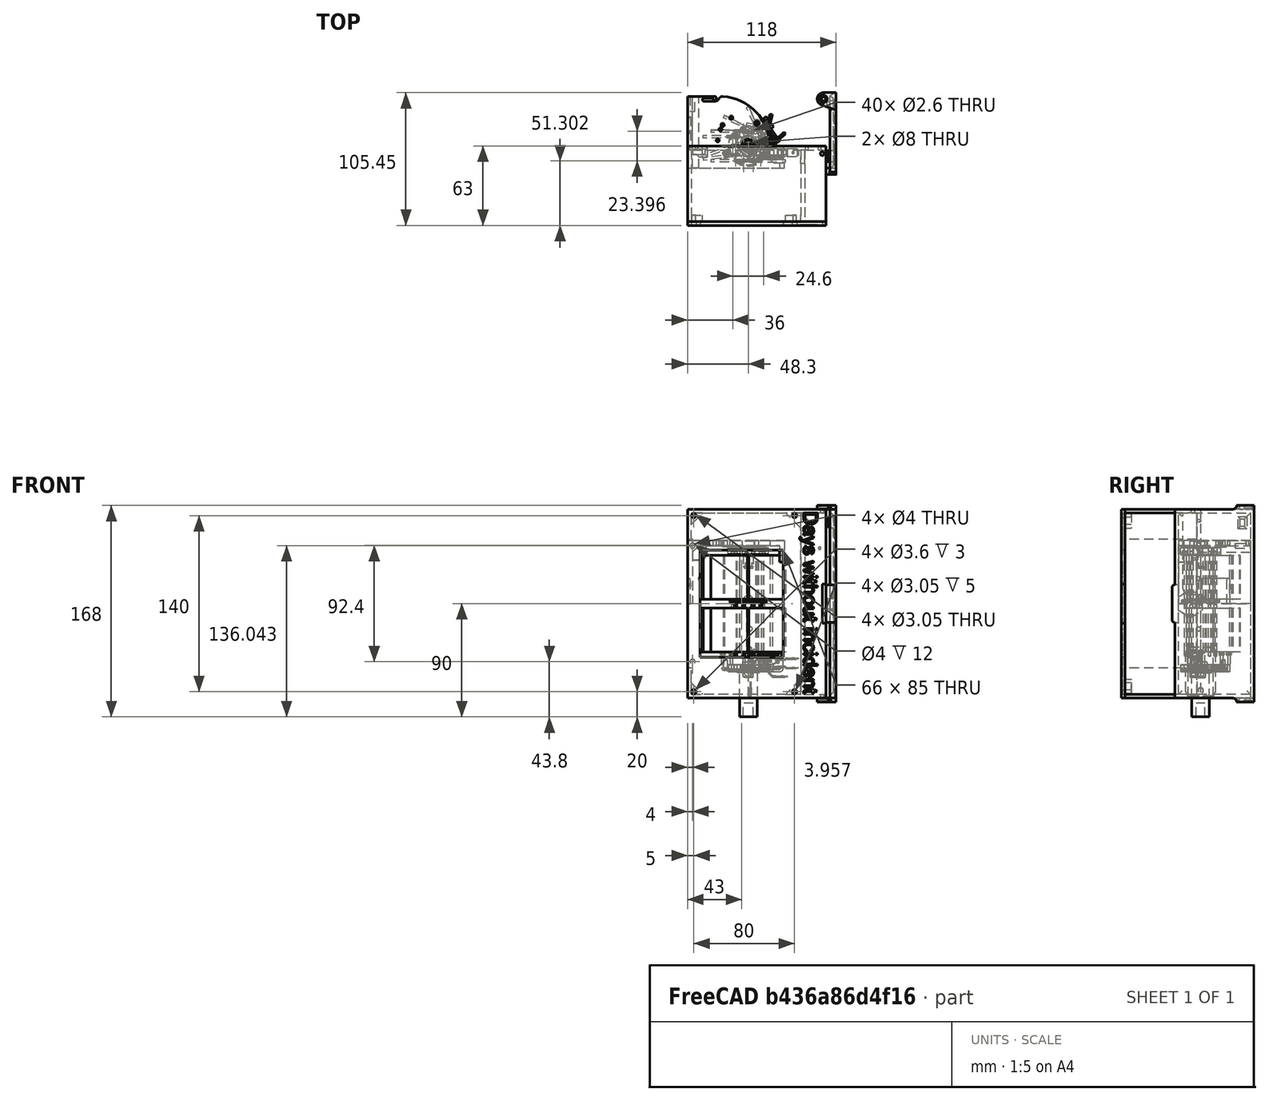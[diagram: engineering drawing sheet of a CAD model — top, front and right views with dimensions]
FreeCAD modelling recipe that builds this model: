
FCSTD DOCUMENT  (FreeCAD 1.0R39285 (Git))
Label: main
License: All rights reserved
LicenseURL: https://en.wikipedia.org/wiki/All_rights_reserved
objects: Sketcher::SketchObject×41, PartDesign::Pad×27, PartDesign::Body×22, Part::Feature×20, PartDesign::Chamfer×12, PartDesign::Pocket×12, App::Part×12, PartDesign::FeatureBase×11, Part::FeaturePython×8, PartDesign::Fillet×4, PartDesign::Revolution×3, PartDesign::Hole×3, PartDesign::PolarPattern×2, Mesh::Feature×1, PartDesign::Mirrored×1, Part::Part2DObjectPython×1, Part::Extrusion×1, PartDesign::LinearPattern×1
note: 347 computed .brp shape members not serialized (recipe doc carries the construction recipe); baked Part::Feature solids carry a one-line shape summary decoded from their .brp

FEATURE [Mesh::Feature] _8BYJ_48_stepper  label="28BYJ-48_stepper"
  Placement = pos=(-37.4756,7.81695,-15) rot=(0.862856,0.357407,0.357407;1.71777rad)
FEATURE [PartDesign::Body] Body  label="frame"
  AllowCompound = false
  Origin = -> Origin001
FEATURE [Sketcher::SketchObject] Sketch
  ArcFitTolerance = 1e-06
  AttachmentSupport = -> [XY_Plane001]
  FullyConstrained = true
  MakeInternals = false
  MapMode = 5
  sketch-geometry (33):
    g0: LineSegment StartX=0 StartY=0 StartZ=0 EndX=76.5 EndY=0 EndZ=0
    g1: LineSegment StartX=77 StartY=0.5 StartZ=0 EndX=77 EndY=3.5 EndZ=0
    g2: LineSegment [constr] StartX=25.5 StartY=57 StartZ=0 EndX=0 EndY=57 EndZ=0
    g3: LineSegment StartX=0 StartY=57 StartZ=0 EndX=0 EndY=0 EndZ=0
    g4: Circle CenterX=48.3 CenterY=17.5 CenterZ=0 NormalX=0 NormalY=0 NormalZ=1 AngleXU=0 Radius=4.8
    g5: Circle CenterX=30.2688 CenterY=10.7825 CenterZ=0 NormalX=0 NormalY=0 NormalZ=1 AngleXU=0 Radius=1.475
    g6: Circle CenterX=55.0175 CenterY=35.5312 CenterZ=0 NormalX=0 NormalY=0 NormalZ=1 AngleXU=0 Radius=1.475
    g7: LineSegment [constr] StartX=55.0175 StartY=35.5312 StartZ=0 EndX=30.2688 EndY=10.7825 EndZ=0
    g8: GeomPoint [constr] X=42.6431 Y=23.1569 Z=0
    g9: LineSegment [constr] StartX=42.6431 StartY=23.1569 StartZ=0 EndX=48.3 EndY=17.5 EndZ=0
    g10: LineSegment StartX=76.5 StartY=4 StartZ=0 EndX=70.5 EndY=4 EndZ=0
    g11: LineSegment StartX=65.5 StartY=9 StartZ=0 EndX=65.5 EndY=17 EndZ=0
    g12: ArcOfCircle CenterX=70.5 CenterY=9 CenterZ=0 NormalX=0 NormalY=0 NormalZ=1 AngleXU=0 Radius=5 StartAngle=3.14159 EndAngle=4.71239
    g13: GeomPoint [constr] X=65.5 Y=4 Z=0
    g14: ArcOfCircle CenterX=76.5 CenterY=0.5 CenterZ=0 NormalX=0 NormalY=0 NormalZ=1 AngleXU=0 Radius=0.5 StartAngle=4.71239 EndAngle=6.28319
    g15: GeomPoint [constr] X=77 Y=0 Z=0
    g16: ArcOfCircle CenterX=76.5 CenterY=3.5 CenterZ=0 NormalX=0 NormalY=0 NormalZ=1 AngleXU=0 Radius=0.5 StartAngle=0 EndAngle=1.5708
    g17: GeomPoint [constr] X=77 Y=4 Z=0
    g18: ArcOfCircle CenterX=25.5 CenterY=17 CenterZ=0 NormalX=0 NormalY=0 NormalZ=1 AngleXU=0 Radius=40 StartAngle=0 EndAngle=1.5708
    g19: GeomPoint [constr] X=65.5 Y=57 Z=0
    g20: Circle [constr] CenterX=55.0175 CenterY=35.5312 CenterZ=0 NormalX=0 NormalY=0 NormalZ=1 AngleXU=0 Radius=3.5
    g21: Circle [constr] CenterX=30.2688 CenterY=10.7825 CenterZ=0 NormalX=0 NormalY=0 NormalZ=1 AngleXU=0 Radius=3.5
    g22: Circle [constr] CenterX=42.6431 CenterY=23.1569 CenterZ=0 NormalX=0 NormalY=0 NormalZ=1 AngleXU=0 Radius=14
    g23: Circle CenterX=27.85 CenterY=34.05 CenterZ=0 NormalX=0 NormalY=0 NormalZ=1 AngleXU=0 Radius=1
    g24: Circle CenterX=34.7319 CenterY=39.85 CenterZ=0 NormalX=0 NormalY=0 NormalZ=1 AngleXU=0 Radius=1
    g25: Circle CenterX=24 CenterY=22 CenterZ=0 NormalX=0 NormalY=0 NormalZ=1 AngleXU=0 Radius=1
    g26: Circle CenterX=26.1879 CenterY=30.73 CenterZ=0 NormalX=0 NormalY=0 NormalZ=1 AngleXU=0 Radius=1
    g27: LineSegment StartX=20 StartY=55.5 StartZ=0 EndX=13 EndY=55.5 EndZ=0
    g28: ArcOfCircle CenterX=13 CenterY=54.3 CenterZ=0 NormalX=0 NormalY=0 NormalZ=1 AngleXU=0 Radius=1.2 StartAngle=1.5708 EndAngle=4.71239
    g29: LineSegment StartX=13 StartY=53.1 StartZ=0 EndX=21.6 EndY=53.1 EndZ=0
    g30: ArcOfCircle CenterX=21.6 CenterY=57 CenterZ=0 NormalX=0 NormalY=0 NormalZ=1 AngleXU=0 Radius=3.9 StartAngle=4.71239 EndAngle=6.28319
    g31: LineSegment StartX=21.5 StartY=57 StartZ=0 EndX=0 EndY=57 EndZ=0
    g32: ArcOfCircle CenterX=21.5 CenterY=55.5 CenterZ=0 NormalX=0 NormalY=0 NormalZ=1 AngleXU=0 Radius=1.5 StartAngle=3.14159 EndAngle=7.85399
  constraints (82):
    c: Coincident(g2,g3)
    c: Coincident(g3,g0)
    c: Horizontal(g0)
    c: Horizontal(g2)
    c: Vertical(g1)
    c: Vertical(g3)
    c: Distance(g15,g3) = 77
    c: Distance(g0,g2) = 57
    c: Coincident(g0,g-1)
    c: Diameter(g4) = 9.6
    c: Equal(g5,g6)
    c: Distance(g5,g6) = 35
    c: Coincident(g7,g6)
    c: Coincident(g7,g5)
    c: Symmetric(g7,g7,g8)
    c: Coincident(g9,g8)
    c: Coincident(g9,g4)
    c: Perpendicular(g7,g9)
    c: Distance(g9,g9) = 8
    c: Angle(g0,g7) = 0.785398
    c: Distance(g4,g3) = 48.3
    c: Distance(g4,g0) = 17.5
    c: Horizontal(g10)
    c: Vertical(g11)
    c: DistanceY(g15,g17) = 4
    c: DistanceX(g13,g17) = 11.5
    c: PointOnObject(g13,g10)
    c: PointOnObject(g13,g11)
    c: Tangent(g10,g12) = 1.5708
    c: Tangent(g11,g12) = 1.5708
    c: Radius(g12) = 5
    c: PointOnObject(g15,g0)
    c: PointOnObject(g15,g1)
    c: Tangent(g0,g14) = -1.5708
    c: Tangent(g1,g14) = -1.5708
    c: PointOnObject(g17,g1)
    c: PointOnObject(g17,g10)
    c: Tangent(g1,g16) = -1.5708
    c: Tangent(g10,g16) = -1.5708
    c: PointOnObject(g19,g2)
    c: PointOnObject(g19,g11)
    c: Tangent(g2,g18) = -1.5708
    c: Tangent(g11,g18) = -1.5708
    c: Coincident(g20,g6)
    c: Radius(g18) = 40
    c: Equal(g14,g16)
    c: Radius(g14) = 0.5
    c: Coincident(g21,g5)
    c: Diameter(g22) = 28
    c: Coincident(g22,g8)
    c: Diameter(g5) = 2.95
    c: Equal(g21,g20)
    c: Diameter(g21) = 7
    c: Diameter(g24) = 2
    c: Distance(g24,g23) = 9
    c: Distance(g23,g3) = 27.85
    c: Distance(g23,g0) = 34.05
    c: DistanceY(g23,g24) = 5.8
    c: Distance(g25,g26) = 9
    c: Equal(g24,g23)
    c: Equal(g23,g26)
    c: Equal(g26,g25)
    c: Distance(g25,g0) = 22
    c: Distance(g25,g3) = 24
    c: DistanceY(g25,g26) = 8.73
    c: PointOnObject(g31,g2)
    c: Horizontal(g27)
    c: Horizontal(g29)
    c: PointOnObject(g30,g2)
    c: Coincident(g30,g2)
    c: Tangent(g28,g27) = -1.5708
    c: Tangent(g29,g28) = -1.5708
    c: Tangent(g30,g29) = -1.5708
    c: Distance(g2,g27) = 1.5
    c: DistanceX(g27,g27) = 7
    c: Radius(g28) = 1.2
    c: DistanceX(g31,g2) = 4
    c: Coincident(g31,g2)
    c: Coincident(g32,g27)
    c: Coincident(g32,g31)
    c: Horizontal(g32,g27)
    c: Radius(g32) = 1.5
FEATURE [PartDesign::Pad] Pad  label="Face_Pad"
  Direction = (0,0,1)
  Length = 4
  Length2 = 10
  Profile = -> Sketch
  ReferenceAxis = -> Sketch [N_Axis]
  Refine = true
  Suppressed = false
  Type = 0
FEATURE [Sketcher::SketchObject] Sketch001
  ArcFitTolerance = 1e-06
  AttachmentSupport = -> [Pad]
  ExternalGeometry = -> [Pad]
  FullyConstrained = true
  MakeInternals = false
  MapMode = 5
  Placement = pos=(0,0,4) rot=(0,0,1;0rad)
  sketch-geometry (8):
    g0: LineSegment StartX=73 StartY=4 StartZ=0 EndX=73 EndY=0 EndZ=0
    g1: LineSegment StartX=73 StartY=0 StartZ=0 EndX=76.5 EndY=0 EndZ=0
    g2: LineSegment StartX=77 StartY=0.5 StartZ=0 EndX=77 EndY=3.5 EndZ=0
    g3: LineSegment StartX=76.5 StartY=4 StartZ=0 EndX=73 EndY=4 EndZ=0
    g4: ArcOfCircle CenterX=76.5 CenterY=3.5 CenterZ=0 NormalX=0 NormalY=0 NormalZ=1 AngleXU=0 Radius=0.5 StartAngle=2e-16 EndAngle=1.5708
    g5: GeomPoint [constr] X=77 Y=4 Z=0
    g6: ArcOfCircle CenterX=76.5 CenterY=0.5 CenterZ=0 NormalX=0 NormalY=0 NormalZ=1 AngleXU=0 Radius=0.5 StartAngle=4.71239 EndAngle=6.28319
    g7: GeomPoint [constr] X=77 Y=0 Z=0
  constraints (19):
    c: Coincident(g0,g1)
    c: Coincident(g3,g0)
    c: Vertical(g0)
    c: Vertical(g2)
    c: Horizontal(g1)
    c: Horizontal(g3)
    c: PointOnObject(g7,g-1)
    c: PointOnObject(g-4,g2)
    c: DistanceX(g3,g5) = 4
    c: PointOnObject(g5,g2)
    c: PointOnObject(g5,g3)
    c: Tangent(g2,g4) = -1.5708
    c: Tangent(g3,g4) = -1.5708
    c: PointOnObject(g7,g1)
    c: PointOnObject(g7,g2)
    c: Tangent(g1,g6) = -1.5708
    c: Tangent(g2,g6) = -1.5708
    c: Equal(g4,g6)
    c: Coincident(g3,g-3)
FEATURE [PartDesign::Pad] Pad001  label="TopStopper_Pad"
  Direction = (0,0,1)
  Length = 13
  Length2 = 10
  Profile = -> Sketch001
  ReferenceAxis = -> Sketch001 [N_Axis]
  Refine = true
  Suppressed = false
  Type = 0
FEATURE [Sketcher::SketchObject] Sketch002
  ArcFitTolerance = 1e-06
  AttachmentSupport = -> [Pad]
  FullyConstrained = true
  MakeInternals = false
  MapMode = 5
  Placement = pos=(0,0,4) rot=(0,0,1;0rad)
  sketch-geometry (4):
    g0: LineSegment StartX=0 StartY=11 StartZ=0 EndX=14 EndY=11 EndZ=0
    g1: LineSegment StartX=14 StartY=11 StartZ=0 EndX=14 EndY=15 EndZ=0
    g2: LineSegment StartX=14 StartY=15 StartZ=0 EndX=0 EndY=15 EndZ=0
    g3: LineSegment StartX=0 StartY=15 StartZ=0 EndX=0 EndY=11 EndZ=0
  constraints (12):
    c: Coincident(g0,g1)
    c: Coincident(g1,g2)
    c: Coincident(g2,g3)
    c: Coincident(g3,g0)
    c: Horizontal(g0)
    c: Horizontal(g2)
    c: Vertical(g1)
    c: Vertical(g3)
    c: Distance(g1,g3) = 14
    c: Distance(g0,g2) = 4
    c: PointOnObject(g0,g-2)
    c: Distance(g-1,g0) = 11
FEATURE [PartDesign::Pad] Pad002  label="BottomStopper_Pad"
  Direction = (0,0,1)
  Length = 11.5
  Length2 = 10
  Profile = -> Sketch002
  ReferenceAxis = -> Sketch002 [N_Axis]
  Refine = true
  Suppressed = false
  Type = 0
FEATURE [PartDesign::Chamfer] Chamfer  label="BottomStopper_Chamfer"
  Angle = 45
  Base = -> Pad002 [Edge3,Edge6,Edge9,Edge7]
  ChamferType = 0
  FlipDirection = false
  Refine = true
  Size = 2
  Size2 = 1
  SupportTransform = false
  Suppressed = false
  UseAllEdges = false
FEATURE [Sketcher::SketchObject] Sketch003
  ArcFitTolerance = 1e-06
  AttachmentSupport = -> [Chamfer]
  ExternalGeometry = -> [Chamfer]
  FullyConstrained = true
  MakeInternals = false
  MapMode = 5
  Placement = pos=(0,0,4) rot=(0,0,1;0rad)
  sketch-geometry (4):
    g0: LineSegment StartX=0 StartY=0 StartZ=0 EndX=4 EndY=0 EndZ=0
    g1: LineSegment StartX=4 StartY=0 StartZ=0 EndX=4 EndY=57 EndZ=0
    g2: LineSegment StartX=4 StartY=57 StartZ=0 EndX=0 EndY=57 EndZ=0
    g3: LineSegment StartX=0 StartY=57 StartZ=0 EndX=0 EndY=0 EndZ=0
  constraints (11):
    c: Coincident(g0,g1)
    c: Coincident(g1,g2)
    c: Coincident(g2,g3)
    c: Coincident(g3,g0)
    c: Horizontal(g0)
    c: Horizontal(g2)
    c: Vertical(g1)
    c: Vertical(g3)
    c: Coincident(g0,g-1)
    c: PointOnObject(g1,g-3)
    c: DistanceX(g2,g2) = 4
FEATURE [PartDesign::Pad] Pad003  label="Bottom_Pad"
  Direction = (0,0,1)
  Length = 46
  Length2 = 10
  Profile = -> Sketch003
  ReferenceAxis = -> Sketch003 [N_Axis]
  Refine = true
  Suppressed = false
  Type = 0
FEATURE [PartDesign::Chamfer] Chamfer001  label="Bottom_Chamfer"
  Angle = 45
  Base = -> Pad003 [Edge4,Edge17]
  ChamferType = 0
  FlipDirection = false
  Refine = true
  Size = 5
  Size2 = 1
  SupportTransform = false
  Suppressed = false
  UseAllEdges = false
FEATURE [Sketcher::SketchObject] Sketch004
  ArcFitTolerance = 1e-06
  AttachmentSupport = -> [XY_Plane003]
  FullyConstrained = true
  MakeInternals = false
  MapMode = 5
  sketch-geometry (6):
    g0: LineSegment StartX=0 StartY=0 StartZ=0 EndX=12 EndY=0 EndZ=0
    g1: LineSegment StartX=12 StartY=0 StartZ=0 EndX=12 EndY=10 EndZ=0
    g2: LineSegment StartX=12 StartY=10 StartZ=0 EndX=0 EndY=10 EndZ=0
    g3: LineSegment StartX=0 StartY=10 StartZ=0 EndX=0 EndY=0 EndZ=0
    g4: Circle CenterX=2.05 CenterY=2.17159 CenterZ=0 NormalX=0 NormalY=0 NormalZ=1 AngleXU=0 Radius=1.05
    g5: Circle CenterX=8.95 CenterY=7.95 CenterZ=0 NormalX=0 NormalY=0 NormalZ=1 AngleXU=0 Radius=1.05
  constraints (17):
    c: Coincident(g0,g1)
    c: Coincident(g1,g2)
    c: Coincident(g2,g3)
    c: Coincident(g3,g0)
    c: Horizontal(g0)
    c: Horizontal(g2)
    c: Vertical(g1)
    c: Vertical(g3)
    c: Distance(g1,g3) = 12
    c: Distance(g0,g2) = 10
    c: Coincident(g0,g-1)
    c: Equal(g5,g4)
    c: Diameter(g4) = 2.1
    c: Distance(g4,g5) = 9
    c: Distance(g5,g1) = 2
    c: Distance(g5,g2) = 1
    c: Distance(g4,g3) = 1
FEATURE [PartDesign::Pad] Pad004  label="Body_Pad"
  Direction = (0,0,1)
  Length = 5.4
  Length2 = 10
  Profile = -> Sketch004
  ReferenceAxis = -> Sketch004 [N_Axis]
  Refine = true
  Suppressed = false
  Type = 0
FEATURE [Sketcher::SketchObject] Sketch005
  ArcFitTolerance = 1e-06
  AttachmentSupport = -> [XY_Plane003]
  ExternalGeometry = -> [Pad004]
  FullyConstrained = true
  MakeInternals = false
  MapMode = 5
  sketch-geometry (6):
    g0: LineSegment StartX=-4.24264 StartY=12.8284 StartZ=0 EndX=0.353553 EndY=8.23223 EndZ=0
    g1: LineSegment StartX=0.353553 StartY=8.23223 StartZ=0 EndX=1.76777 EndY=9.64645 EndZ=0
    g2: LineSegment StartX=1.76777 StartY=9.64645 StartZ=0 EndX=-2.82843 EndY=14.2426 EndZ=0
    g3: ArcOfCircle CenterX=-3.53553 CenterY=13.5355 CenterZ=0 NormalX=0 NormalY=0 NormalZ=1 AngleXU=0 Radius=1 StartAngle=0.785398 EndAngle=3.92699
    g4: GeomPoint X=1.06066 Y=8.93934 Z=0
    g5: LineSegment [constr] StartX=0 StartY=10 StartZ=0 EndX=1.06066 EndY=8.93934 EndZ=0
  constraints (14):
    c: Coincident(g0,g1)
    c: Coincident(g1,g2)
    c: Tangent(g3,g0) = -1.5708
    c: Tangent(g3,g2) = -1.5708
    c: Equal(g0,g2)
    c: Radius(g3) = 1
    c: Parallel(g0,g2)
    c: Angle(g-2,g2) = 0.785398
    c: Distance(g2,g2) = 6.5
    c: Symmetric(g1,g1,g4)
    c: Coincident(g5,g-3)
    c: Coincident(g5,g4)
    c: Distance(g5,g5) = 1.5
    c: Angle(g-2,g5) = 0.785398
FEATURE [PartDesign::Pad] Pad005  label="LeverOFF_Pad"
  BaseFeature = -> Pad004
  Direction = (0,0,1)
  Length = 4.4
  Length2 = -1
  Profile = -> Sketch005
  ReferenceAxis = -> Sketch005 [N_Axis]
  Refine = true
  Suppressed = false
  Type = 4
FEATURE [Sketcher::SketchObject] Sketch006
  ArcFitTolerance = 1e-06
  AttachmentSupport = -> [Pad005]
  ExternalGeometry = -> [Pad005]
  FullyConstrained = true
  MakeInternals = false
  MapMode = 5
  Placement = pos=(0,0,0) rot=(1,0,0;1.5708rad)
  sketch-geometry (6):
    g0: GeomPoint X=12 Y=2.7 Z=0
    g1: LineSegment [constr] StartX=12 StartY=2.7 StartZ=0 EndX=0 EndY=2.7 EndZ=0
    g2: Circle CenterX=3.5 CenterY=2.7 CenterZ=0 NormalX=0 NormalY=0 NormalZ=1 AngleXU=0 Radius=1
    g3: Circle CenterX=6 CenterY=2.7 CenterZ=0 NormalX=0 NormalY=0 NormalZ=1 AngleXU=0 Radius=1
    g4: Circle CenterX=8.5 CenterY=2.7 CenterZ=0 NormalX=0 NormalY=0 NormalZ=1 AngleXU=0 Radius=1
    g5: GeomPoint X=6 Y=2.7 Z=0
  constraints (13):
    c: Symmetric(g-3,g-3,g0)
    c: Coincident(g1,g0)
    c: Horizontal(g1)
    c: Diameter(g2) = 2
    c: PointOnObject(g2,g1)
    c: PointOnObject(g4,g1)
    c: Equal(g4,g3)
    c: Equal(g3,g2)
    c: DistanceX(g2,g3) = 2.5
    c: DistanceX(g3,g4) = 2.5
    c: Symmetric(g1,g1,g5)
    c: Coincident(g5,g3)
    c: PointOnObject(g1,g-2)
FEATURE [PartDesign::Pad] Pad006  label="Wires_Pad"
  BaseFeature = -> Pad005
  Direction = (0,-1,2e-16)
  Length = 12
  Length2 = 10
  Profile = -> Sketch006
  ReferenceAxis = -> Sketch006 [N_Axis]
  Refine = true
  Suppressed = false
  Type = 0
FEATURE [Sketcher::SketchObject] Sketch007
  ArcFitTolerance = 1e-06
  AttachmentSupport = -> [XY_Plane003]
  ExternalGeometry = -> [Pad004]
  FullyConstrained = true
  MakeInternals = false
  MapMode = 5
  sketch-geometry (6):
    g0: LineSegment StartX=1.06066 StartY=7.93934 StartZ=0 EndX=-5.43934 EndY=7.93934 EndZ=0
    g1: LineSegment StartX=-5.43934 StartY=9.93934 StartZ=0 EndX=1.06066 EndY=9.93934 EndZ=0
    g2: LineSegment StartX=1.06066 StartY=7.93934 StartZ=0 EndX=1.06066 EndY=9.93934 EndZ=0
    g3: ArcOfCircle CenterX=-5.43934 CenterY=8.93934 CenterZ=0 NormalX=0 NormalY=0 NormalZ=1 AngleXU=0 Radius=1 StartAngle=1.5708 EndAngle=4.71239
    g4: LineSegment [constr] StartX=0 StartY=10 StartZ=0 EndX=1.06066 EndY=8.93934 EndZ=0
    g5: GeomPoint [constr] X=1.06066 Y=8.93934 Z=0
  constraints (14):
    c: Horizontal(g0)
    c: Horizontal(g1)
    c: Coincident(g2,g0)
    c: Coincident(g2,g1)
    c: Vertical(g2)
    c: Tangent(g3,g1) = 1.5708
    c: Tangent(g3,g0) = 1.5708
    c: Radius(g3) = 1
    c: DistanceX(g1,g1) = 6.5
    c: Distance(g4) = 1.5
    c: Angle(g-1,g4) = -0.785398
    c: Coincident(g4,g-3)
    c: Symmetric(g2,g2,g5)
    c: Coincident(g5,g4)
FEATURE [PartDesign::Pad] Pad007  label="LeverON_Pad"
  BaseFeature = -> Pad006
  Direction = (0,0,1)
  Length = 4.4
  Length2 = -1
  Profile = -> Sketch007
  ReferenceAxis = -> Sketch007 [N_Axis]
  Refine = true
  Suppressed = false
  Type = 4
FEATURE [PartDesign::Body] Body001  label="Body"
  AllowCompound = false
  Group = -> [Sketch004,Pad004,Sketch005,Pad005,Sketch006,Pad006,Sketch007,Pad007]
  Origin = -> Origin003
  Tip = -> Pad007
FEATURE [Sketcher::SketchObject] Sketch008
  ArcFitTolerance = 1e-06
  AttachmentSupport = -> [XY_Plane005]
  FullyConstrained = true
  MakeInternals = false
  MapMode = 5
  sketch-geometry (6):
    g0: Circle CenterX=0 CenterY=0 CenterZ=0 NormalX=0 NormalY=0 NormalZ=1 AngleXU=0 Radius=16
    g1: LineSegment StartX=-2.55 StartY=-1.55 StartZ=0 EndX=2.55 EndY=-1.55 EndZ=0
    g2: LineSegment StartX=2.55 StartY=-1.55 StartZ=0 EndX=2.55 EndY=1.55 EndZ=0
    g3: LineSegment StartX=2.55 StartY=1.55 StartZ=0 EndX=-2.55 EndY=1.55 EndZ=0
    g4: LineSegment StartX=-2.55 StartY=1.55 StartZ=0 EndX=-2.55 EndY=-1.55 EndZ=0
    g5: GeomPoint [constr] X=0 Y=0 Z=0
  constraints (14):
    c: Coincident(g0,g-1)
    c: Coincident(g1,g2)
    c: Coincident(g2,g3)
    c: Coincident(g3,g4)
    c: Coincident(g4,g1)
    c: Horizontal(g1)
    c: Horizontal(g3)
    c: Vertical(g2)
    c: Vertical(g4)
    c: Symmetric(g3,g1,g5)
    c: Distance(g2,g4) = 5.1
    c: Distance(g1,g3) = 3.1
    c: Coincident(g5,g0)
    c: Diameter(g0) = 32
FEATURE [PartDesign::Pad] Pad008  label="Flange_Pad001"
  Direction = (0,0,1)
  Length = 5.5
  Length2 = 10
  Profile = -> Sketch008
  ReferenceAxis = -> Sketch008 [N_Axis]
  Refine = true
  Suppressed = false
  Type = 0
FEATURE [Sketcher::SketchObject] Sketch009
  ArcFitTolerance = 1e-06
  AttachmentSupport = -> [Chamfer001]
  ExternalGeometry = -> [Chamfer001]
  FullyConstrained = true
  MakeInternals = false
  MapMode = 5
  Placement = pos=(0,0,4) rot=(0,0,1;0rad)
  sketch-geometry (2):
    g0: Circle CenterX=48.3 CenterY=17.5 CenterZ=0 NormalX=0 NormalY=0 NormalZ=1 AngleXU=0 Radius=4.8
    g1: Circle CenterX=48.3 CenterY=17.5 CenterZ=0 NormalX=0 NormalY=0 NormalZ=1 AngleXU=0 Radius=7.3
  constraints (4):
    c: Coincident(g0,g-3)
    c: Equal(g0,g-3)
    c: Coincident(g1,g0)
    c: Distance(g0,g1) = 2.5
FEATURE [PartDesign::Pad] Pad009  label="Flange_Pad"
  Direction = (0,0,1)
  Length = 1.75
  Length2 = 10
  Profile = -> Sketch009
  ReferenceAxis = -> Sketch009 [N_Axis]
  Refine = true
  Suppressed = false
  Type = 0
FEATURE [PartDesign::Chamfer] Chamfer002  label="Flange_Chamfer"
  Angle = 45
  Base = -> Pad009 [Edge76,Edge107,Edge20,Edge103]
  ChamferType = 0
  FlipDirection = false
  Refine = true
  Size = 0.5
  Size2 = 1
  SupportTransform = false
  Suppressed = false
  UseAllEdges = false
FEATURE [Sketcher::SketchObject] Sketch010
  ArcFitTolerance = 1e-06
  AttachmentSupport = -> [Pad008]
  FullyConstrained = true
  MakeInternals = false
  MapMode = 5
  Placement = pos=(0,0,5.5) rot=(0,0,1;0rad)
  sketch-geometry (1):
    g0: Circle CenterX=12.3 CenterY=0 CenterZ=0 NormalX=0 NormalY=0 NormalZ=1 AngleXU=0 Radius=1.3
  constraints (3):
    c: Diameter(g0) = 2.6
    c: PointOnObject(g0,g-1)
    c: Distance(g-1,g0) = 11
FEATURE [PartDesign::Pocket] Pocket  label="Flap_Pocket"
  BaseFeature = -> Pad008
  Direction = (0,0,-1)
  Length = 5
  Length2 = 5
  Profile = -> Sketch010
  ReferenceAxis = -> Sketch010 [N_Axis]
  Refine = true
  Suppressed = false
  Type = 2
FEATURE [PartDesign::Chamfer] Chamfer003  label="FlapHole_Chamfer"
  Angle = 45
  Base = -> Pocket [Edge13,Edge8]
  BaseFeature = -> Pocket
  ChamferType = 0
  FlipDirection = false
  Refine = true
  Size = 0.2
  Size2 = 1
  SupportTransform = false
  Suppressed = false
  UseAllEdges = false
FEATURE [PartDesign::PolarPattern] PolarPattern  label="Flap_PolarPattern"
  Angle = 360
  Axis = -> Z_Axis005
  BaseFeature = -> Chamfer003
  Mode = 0
  Occurrences = 10
  Offset = 120
  Originals = -> [Pocket,Chamfer003]
  Refine = true
  Suppressed = false
  TransformMode = 0
FEATURE [PartDesign::FeatureBase] Clone
  BaseFeature = -> Body001
  Suppressed = false
FEATURE [PartDesign::Body] Body003  label="Copy"
  AllowCompound = false
  Group = -> [Clone]
  Origin = -> Origin006
  Placement = pos=(10.2368,8.31942,0) rot=(0,0,-1;5.65487rad)
  Tip = -> Clone
FEATURE [App::Part] Part001  label="MicroSW"
  Group = -> [Body001,Body003]
  Origin = -> Origin002
  Placement = pos=(-11.5,24.5,8) rot=(0,0,-1;3.14159rad)
FEATURE [Sketcher::SketchObject] Sketch012
  ArcFitTolerance = 1e-06
  AttachmentSupport = -> [Chamfer002]
  ExternalGeometry = -> [Chamfer002]
  FullyConstrained = true
  MakeInternals = false
  MapMode = 5
  Placement = pos=(0,0,4) rot=(0,0,1;0rad)
  sketch-geometry (4):
    g0: Circle CenterX=55.0175 CenterY=35.5312 CenterZ=0 NormalX=0 NormalY=0 NormalZ=1 AngleXU=0 Radius=1.525
    g1: Circle CenterX=55.0175 CenterY=35.5312 CenterZ=0 NormalX=0 NormalY=0 NormalZ=1 AngleXU=0 Radius=2.525
    g2: Circle CenterX=30.2688 CenterY=10.7825 CenterZ=0 NormalX=0 NormalY=0 NormalZ=1 AngleXU=0 Radius=1.525
    g3: Circle CenterX=30.2688 CenterY=10.7825 CenterZ=0 NormalX=0 NormalY=0 NormalZ=1 AngleXU=0 Radius=2.525
  constraints (8):
    c: Coincident(g0,g-4)
    c: Equal(g0,g-4)
    c: Coincident(g1,g0)
    c: Coincident(g2,g-3)
    c: Equal(g2,g-3)
    c: Coincident(g3,g2)
    c: Equal(g3,g1)
    c: Distance(g0,g1) = 1
FEATURE [PartDesign::Pad] Pad010  label="MotorHole_Pad"
  Direction = (0,0,1)
  Length = 1
  Length2 = 10
  Profile = -> Sketch012
  ReferenceAxis = -> Sketch012 [N_Axis]
  Refine = true
  Suppressed = false
  Type = 0
FEATURE [PartDesign::Chamfer] Chamfer005  label="TinyHoles_Chamfer"
  Angle = 45
  Base = -> Pad010 [Edge19,Edge21,Edge22,Edge23,Edge24,Edge18,Edge72,Edge84,Edge74,Edge104,Edge105,Edge82,Edge80,Edge78]
  ChamferType = 0
  FlipDirection = false
  Refine = true
  Size = 0.2
  Size2 = 1
  SupportTransform = false
  Suppressed = false
  UseAllEdges = false
FEATURE [Sketcher::SketchObject] Sketch013
  ArcFitTolerance = 1e-06
  AttachmentSupport = -> [Chamfer005]
  ExternalGeometry = -> [Chamfer005]
  FullyConstrained = true
  MakeInternals = false
  MapMode = 5
  Placement = pos=(0,0,50) rot=(0,0,1;0rad)
  sketch-geometry (6):
    g0: GeomPoint X=0 Y=28.5 Z=0
    g1: LineSegment StartX=0 StartY=38.5 StartZ=0 EndX=0 EndY=18.5 EndZ=0
    g2: GeomPoint X=0 Y=28.5 Z=0
    g3: LineSegment StartX=0 StartY=38.5 StartZ=0 EndX=2.5 EndY=41 EndZ=0
    g4: LineSegment StartX=2.5 StartY=41 StartZ=0 EndX=2.5 EndY=16 EndZ=0
    g5: LineSegment StartX=2.5 StartY=16 StartZ=0 EndX=0 EndY=18.5 EndZ=0
  constraints (13):
    c: Symmetric(g-3,g-3,g0)
    c: PointOnObject(g1,g-3)
    c: Symmetric(g1,g1,g2)
    c: Coincident(g2,g0)
    c: Coincident(g3,g1)
    c: Coincident(g4,g3)
    c: Vertical(g4)
    c: Coincident(g5,g4)
    c: Coincident(g5,g1)
    c: Equal(g5,g3)
    c: Distance(g4,g1) = 2.5
    c: Angle(g4,g5) = 0.785398
    c: DistanceY(g4,g4) = 25
FEATURE [PartDesign::Pocket] Pocket002  label="LeftRightJoint_Pocket"
  Direction = (0,0,-1)
  Length = 20
  Length2 = 5
  Profile = -> Sketch013
  ReferenceAxis = -> Sketch013 [N_Axis]
  Refine = true
  Suppressed = false
  Type = 0
FEATURE [Sketcher::SketchObject] Sketch014
  ArcFitTolerance = 1e-06
  AttachmentOffset = pos=(0,0,-1) rot=(0,0,1;0rad)
  AttachmentSupport = -> [Pocket002]
  ExternalGeometry = -> [Pocket002]
  FullyConstrained = true
  MakeInternals = false
  MapMode = 5
  Placement = pos=(3.5,0,0) rot=(0.57735,-0.57735,-0.57735;2.0944rad)
  sketch-geometry (5):
    g0: GeomPoint X=-28.5 Y=50 Z=0
    g1: LineSegment [constr] StartX=-28.5 StartY=50 StartZ=0 EndX=-28.5 EndY=35 EndZ=0
    g2: LineSegment StartX=-28.5 StartY=37 StartZ=0 EndX=-28.5 EndY=33 EndZ=0
    g3: GeomPoint X=-28.5 Y=35 Z=0
    g4: ArcOfCircle CenterX=-28.5 CenterY=35 CenterZ=0 NormalX=0 NormalY=0 NormalZ=1 AngleXU=0 Radius=2 StartAngle=1.5708 EndAngle=4.71239
  constraints (11):
    c: Symmetric(g-3,g-3,g0)
    c: Distance(g1) = 15
    c: Coincident(g1,g0)
    c: Vertical(g1)
    c: PointOnObject(g2,g1)
    c: Symmetric(g2,g2,g3)
    c: Coincident(g3,g1)
    c: DistanceY(g2,g2) = 4
    c: Coincident(g4,g2)
    c: Coincident(g4,g1)
    c: PointOnObject(g4,g1)
FEATURE [PartDesign::Revolution] Revolution  label="JointIndent_Revolution"
  Angle = 180
  Angle2 = 60
  Axis = (0,0,-15)
  Base = (3.5,28.5,50)
  Profile = -> Sketch014
  ReferenceAxis = -> Sketch014 [Axis]
  Refine = true
  Reversed = true
  Suppressed = false
  Type = 0
FEATURE [Sketcher::SketchObject] Sketch015
  ArcFitTolerance = 1e-06
  AttachmentSupport = -> [XY_Plane008]
  FullyConstrained = true
  MakeInternals = false
  MapMode = 5
  expr: Constraints[21] = 25 / 2 - 0.1
  sketch-geometry (9):
    g0: LineSegment StartX=4.47e-14 StartY=-10.1 StartZ=0 EndX=-4.52e-14 EndY=10.1 EndZ=0
    g1: LineSegment StartX=-4.52e-14 StartY=10.1 StartZ=0 EndX=1.8 EndY=11.9 EndZ=0
    g2: LineSegment StartX=1.8 StartY=11.9 StartZ=0 EndX=2.3 EndY=11.9 EndZ=0
    g3: LineSegment StartX=2.3 StartY=11.9 StartZ=0 EndX=2.3 EndY=-11.9 EndZ=0
    g4: LineSegment StartX=2.3 StartY=-11.9 StartZ=0 EndX=1.8 EndY=-11.9 EndZ=0
    g5: LineSegment StartX=1.8 StartY=-11.9 StartZ=0 EndX=4.46e-14 EndY=-10.1 EndZ=0
    g6: GeomPoint X=-3e-16 Y=-2.8e-15 Z=0
    g7: LineSegment [constr] StartX=1.8 StartY=-11.9 StartZ=0 EndX=2.3 EndY=-12.4 EndZ=0
    g8: LineSegment [constr] StartX=2.3 StartY=-11.9 StartZ=0 EndX=2.3 EndY=-12.4 EndZ=0
  constraints (24):
    c: PointOnObject(g0,g-2)
    c: PointOnObject(g0,g-2)
    c: Coincident(g0,g1)
    c: Coincident(g1,g2)
    c: Horizontal(g2)
    c: Coincident(g2,g3)
    c: Vertical(g3)
    c: Coincident(g3,g4)
    c: Coincident(g4,g5)
    c: Coincident(g5,g0)
    c: Horizontal(g4)
    c: Equal(g2,g4)
    c: Equal(g5,g1)
    c: Angle(g1,g3) = 0.785398
    c: Symmetric(g0,g0,g6)
    c: Distance(g4,g4) = 0.5
    c: Coincident(g7,g4)
    c: Coincident(g8,g7)
    c: Vertical(g8)
    c: Parallel(g7,g5)
    c: Coincident(g8,g3)
    c: DistanceY(g7,g6) = 12.4
    c: Distance(g3,g0) = 2.3
    c: PointOnObject(g6,g-1)
FEATURE [PartDesign::Pad] Pad011
  Direction = (0,0,1)
  Length = 39
  Length2 = 10
  Midplane = true
  Profile = -> Sketch015
  ReferenceAxis = -> Sketch015 [N_Axis]
  Refine = true
  Suppressed = false
  Type = 0
FEATURE [Sketcher::SketchObject] Sketch016
  ArcFitTolerance = 1e-06
  AttachmentSupport = -> [Pad011]
  FullyConstrained = true
  MakeInternals = false
  MapMode = 5
  Placement = pos=(2.3,0,0) rot=(0.57735,0.57735,0.57735;2.0944rad)
  sketch-geometry (2):
    g0: Circle CenterX=0 CenterY=15 CenterZ=0 NormalX=0 NormalY=0 NormalZ=1 AngleXU=0 Radius=2
    g1: Circle CenterX=0 CenterY=-15 CenterZ=0 NormalX=0 NormalY=0 NormalZ=1 AngleXU=0 Radius=2
  constraints (5):
    c: Diameter(g0) = 4
    c: PointOnObject(g0,g-2)
    c: Diameter(g1) = 4
    c: Symmetric(g0,g1,g-1)
    c: Distance(g1,g-1) = 15
FEATURE [PartDesign::Pocket] Pocket003
  BaseFeature = -> Pad011
  Direction = (-1,0,0)
  Length = 5
  Length2 = 5
  Profile = -> Sketch016
  ReferenceAxis = -> Sketch016 [N_Axis]
  Refine = true
  Suppressed = false
  Type = 2
FEATURE [PartDesign::Chamfer] Chamfer006
  Angle = 45
  Base = -> Pocket003 [Edge13,Edge11,Edge17,Edge15]
  BaseFeature = -> Pocket003
  ChamferType = 1
  FlipDirection = false
  Refine = true
  Size = 1.5
  Size2 = 4
  SupportTransform = false
  Suppressed = false
  UseAllEdges = false
FEATURE [PartDesign::Chamfer] Chamfer007
  Angle = 45
  Base = -> Chamfer006 [Edge29,Edge24,Edge28,Edge23]
  BaseFeature = -> Chamfer006
  ChamferType = 0
  FlipDirection = false
  Refine = true
  Size = 0.2
  Size2 = 1
  SupportTransform = false
  Suppressed = false
  UseAllEdges = false
FEATURE [PartDesign::Body] Body004
  AllowCompound = false
  Group = -> [Sketch015,Pad011,Sketch016,Pocket003,Chamfer006,Chamfer007]
  Origin = -> Origin008
  Tip = -> Chamfer007
FEATURE [App::Part] Part003  label="JointKey"
  Group = -> [Body004]
  Origin = -> Origin007
  Placement = pos=(-48.1,11,54) rot=(0,0,1;0rad)
FEATURE [Sketcher::SketchObject] Sketch017
  ArcFitTolerance = 1e-06
  AttachmentSupport = -> [XY_Plane010]
  FullyConstrained = true
  MakeInternals = false
  MapMode = 5
  sketch-geometry (1):
    g0: Circle CenterX=0 CenterY=0 CenterZ=0 NormalX=0 NormalY=0 NormalZ=1 AngleXU=0 Radius=15
  constraints (2):
    c: Diameter(g0) = 30
    c: Coincident(g0,g-1)
FEATURE [PartDesign::Pad] Pad012  label="Base_Pad"
  Direction = (0,0,1)
  Length = 2
  Length2 = 10
  Profile = -> Sketch017
  ReferenceAxis = -> Sketch017 [N_Axis]
  Refine = true
  Suppressed = false
  Type = 0
FEATURE [Sketcher::SketchObject] Sketch018
  ArcFitTolerance = 1e-06
  AttachmentSupport = -> [Pad012]
  FullyConstrained = true
  MakeInternals = false
  MapMode = 5
  Placement = pos=(0,0,0) rot=(1,0,0;3.14159rad)
  sketch-geometry (1):
    g0: Circle CenterX=12.3 CenterY=0 CenterZ=0 NormalX=0 NormalY=0 NormalZ=1 AngleXU=0 Radius=1.3
  constraints (3):
    c: Diameter(g0) = 2.6
    c: PointOnObject(g0,g-1)
    c: Distance(g-1,g0) = 11
FEATURE [PartDesign::Pocket] Pocket004  label="Flap_Pocket001"
  BaseFeature = -> Pad012
  Direction = (0,0,1)
  Length = 5
  Length2 = 5
  Profile = -> Sketch018
  ReferenceAxis = -> Sketch018 [N_Axis]
  Refine = true
  Suppressed = false
  Type = 2
FEATURE [PartDesign::Chamfer] Chamfer008  label="FlapPocket_Chamfer"
  Angle = 45
  Base = -> Pocket004 [Edge4,Edge5]
  BaseFeature = -> Pocket004
  ChamferType = 0
  FlipDirection = false
  Refine = true
  Size = 0.2
  Size2 = 1
  SupportTransform = false
  Suppressed = false
  UseAllEdges = false
FEATURE [PartDesign::PolarPattern] PolarPattern001  label="Flap_PolarPattern001"
  Angle = 360
  Axis = -> Z_Axis010
  BaseFeature = -> Chamfer008
  Mode = 0
  Occurrences = 10
  Offset = 120
  Originals = -> [Pocket004,Chamfer008]
  Refine = true
  Suppressed = false
  TransformMode = 0
FEATURE [Sketcher::SketchObject] Sketch019
  ArcFitTolerance = 1e-06
  AttachmentSupport = -> [PolarPattern001]
  FullyConstrained = true
  MakeInternals = false
  MapMode = 5
  Placement = pos=(0,0,0) rot=(1,0,0;3.14159rad)
  sketch-geometry (1):
    g0: Circle CenterX=0 CenterY=0 CenterZ=0 NormalX=0 NormalY=0 NormalZ=1 AngleXU=0 Radius=7
  constraints (2):
    c: Diameter(g0) = 14
    c: Coincident(g0,g-1)
FEATURE [PartDesign::Pad] Pad013  label="Shaft_Pad"
  BaseFeature = -> PolarPattern001
  Direction = (0,0,-1)
  Length = 36
  Length2 = 10
  Profile = -> Sketch019
  ReferenceAxis = -> Sketch019 [N_Axis]
  Refine = true
  Suppressed = false
  Type = 0
FEATURE [Sketcher::SketchObject] Sketch021
  ArcFitTolerance = 1e-06
  AttachmentSupport = -> [Pad013]
  FullyConstrained = true
  MakeInternals = false
  MapMode = 5
  Placement = pos=(0,0,-36) rot=(1,0,0;3.14159rad)
  sketch-geometry (5):
    g0: LineSegment StartX=-4 StartY=-3.5 StartZ=0 EndX=4 EndY=-3.5 EndZ=0
    g1: LineSegment StartX=4 StartY=-3.5 StartZ=0 EndX=4 EndY=3.5 EndZ=0
    g2: LineSegment StartX=4 StartY=3.5 StartZ=0 EndX=-4 EndY=3.5 EndZ=0
    g3: LineSegment StartX=-4 StartY=3.5 StartZ=0 EndX=-4 EndY=-3.5 EndZ=0
    g4: GeomPoint [constr] X=0 Y=0 Z=0
  constraints (12):
    c: Coincident(g0,g1)
    c: Coincident(g1,g2)
    c: Coincident(g2,g3)
    c: Coincident(g3,g0)
    c: Horizontal(g0)
    c: Horizontal(g2)
    c: Vertical(g1)
    c: Vertical(g3)
    c: Symmetric(g2,g0,g4)
    c: Distance(g1,g3) = 8
    c: Distance(g0,g2) = 7
    c: Coincident(g4,g-1)
FEATURE [PartDesign::Pocket] Pocket005  label="ShaftKey_Pocket"
  BaseFeature = -> Pad013
  Direction = (0,0,1)
  Length = 11
  Length2 = 5
  Profile = -> Sketch021
  ReferenceAxis = -> Sketch021 [N_Axis]
  Refine = true
  Suppressed = false
  Type = 0
FEATURE [Sketcher::SketchObject] Sketch022
  ArcFitTolerance = 1e-06
  AttachmentSupport = -> [Pocket005]
  FullyConstrained = true
  MakeInternals = false
  MapMode = 5
  Placement = pos=(0,0,2) rot=(0,0,1;0rad)
  sketch-geometry (1):
    g0: Circle CenterX=0 CenterY=0 CenterZ=0 NormalX=0 NormalY=0 NormalZ=1 AngleXU=0 Radius=4
  constraints (2):
    c: Diameter(g0) = 8
    c: Coincident(g0,g-1)
FEATURE [PartDesign::Hole] Hole  label="ShaftLRAlign_Hole"
  BaseFeature = -> Pocket005
  CustomThreadClearance = 0
  Depth = 3
  DepthType = 0
  Diameter = 8
  DrillForDepth = false
  DrillPoint = 1
  DrillPointAngle = 90
  HoleCutCountersinkAngle = 90
  HoleCutCustomValues = false
  HoleCutDepth = 0
  HoleCutDiameter = 13.6
  HoleCutType = 0
  ModelThread = false
  Profile = -> Sketch022
  Refine = true
  Suppressed = false
  Tapered = false
  TaperedAngle = 90
  ThreadClass = 0
  ThreadDepth = 3
  ThreadDepthType = 0
  ThreadDirection = 0
  ThreadFit = 0
  ThreadSize = 0
  ThreadType = 0
  Threaded = false
  UseCustomThreadClearance = false
FEATURE [PartDesign::Chamfer] Chamfer009
  Angle = 45
  Base = -> Hole [Edge44,Edge14,Edge1,Edge30,Edge9,Edge63,Edge62,Edge65,Edge64]
  BaseFeature = -> Hole
  ChamferType = 0
  FlipDirection = false
  Refine = true
  Size = 0.2
  Size2 = 1
  SupportTransform = false
  Suppressed = false
  UseAllEdges = false
FEATURE [PartDesign::Body] Body005
  AllowCompound = false
  Group = -> [Sketch017,Pad012,Sketch018,Pocket004,Chamfer008,PolarPattern001,Sketch019,Pad013,Sketch021,Pocket005,Sketch022,Hole,Chamfer009]
  Origin = -> Origin010
  Tip = -> Chamfer009
FEATURE [App::Part] Part004  label="Drum"
  Group = -> [Body005]
  Origin = -> Origin009
  Placement = pos=(0,0,51) rot=(0,0,1;0rad)
FEATURE [Sketcher::SketchObject] Sketch023
  ArcFitTolerance = 1e-06
  AttachmentSupport = -> [XZ_Plane012]
  FullyConstrained = true
  MakeInternals = false
  MapMode = 5
  Placement = pos=(0,0,0) rot=(1,0,0;1.5708rad)
  expr: Constraints[17] = 17 / 2
  sketch-geometry (8):
    g0: LineSegment StartX=0 StartY=0 StartZ=0 EndX=0 EndY=-4.81036 EndZ=0
    g1: LineSegment StartX=0 StartY=-4.81036 StartZ=0 EndX=3 EndY=-4.81036 EndZ=0
    g2: LineSegment StartX=3 StartY=-4.81036 StartZ=0 EndX=3.9 EndY=-4 EndZ=0
    g3: LineSegment StartX=3.9 StartY=-4 StartZ=0 EndX=3.9 EndY=-1 EndZ=0
    g4: LineSegment StartX=3.9 StartY=-1 StartZ=0 EndX=8.3 EndY=-1 EndZ=0
    g5: LineSegment StartX=8.3 StartY=-1 StartZ=0 EndX=8.5 EndY=-0.8 EndZ=0
    g6: LineSegment StartX=8.5 StartY=-0.8 StartZ=0 EndX=8.5 EndY=0 EndZ=0
    g7: LineSegment StartX=8.5 StartY=0 StartZ=0 EndX=0 EndY=0 EndZ=0
  constraints (23):
    c: Coincident(g-1,g0)
    c: PointOnObject(g0,g-2)
    c: Coincident(g0,g1)
    c: Horizontal(g1)
    c: Coincident(g1,g2)
    c: Coincident(g2,g3)
    c: Vertical(g3)
    c: Coincident(g3,g4)
    c: Horizontal(g4)
    c: Coincident(g4,g5)
    c: Coincident(g5,g6)
    c: PointOnObject(g6,g-1)
    c: Vertical(g6)
    c: Coincident(g6,g7)
    c: Coincident(g7,g0)
    c: Angle(g2,g0) = 0.837758
    c: DistanceY(g3,g3) = 3
    c: DistanceX(g7,g7) = 8.5
    c: Angle(g5,g3) = 0.785398
    c: DistanceX(g4,g5) = 0.2
    c: DistanceX(g-1,g3) = 3.9
    c: DistanceX(g1,g1) = 3
    c: DistanceY(g4,g-1) = 1
FEATURE [PartDesign::Revolution] Revolution001
  Angle = 360
  Angle2 = 60
  Axis = (0,2e-16,1)
  Base = (0,0,0)
  Placement = pos=(0,0,0) rot=(1,0,0;1.5708rad)
  Profile = -> Sketch023
  ReferenceAxis = -> Sketch023 [V_Axis]
  Refine = true
  Reversed = true
  Suppressed = false
  Type = 0
FEATURE [PartDesign::Mirrored] Mirrored
  BaseFeature = -> Revolution001
  MirrorPlane = -> XY_Plane012
  Placement = pos=(0,0,0) rot=(1,0,0;1.5708rad)
  Refine = true
  Suppressed = false
  TransformMode = 1
FEATURE [PartDesign::Body] Body006
  AllowCompound = false
  Group = -> [Sketch023,Revolution001,Mirrored]
  Origin = -> Origin012
  Tip = -> Mirrored
FEATURE [App::Part] Part005  label="JointShaft"
  Group = -> [Body006]
  Origin = -> Origin011
  Placement = pos=(0,0,54) rot=(0,0,1;0rad)
FEATURE [Part::FeaturePython] Screw001  label="M2x8-Screw001"  # WARN: FeaturePython — macro-defined, semantics opaque (R4)
  Diameter = 2
  Invert = false
  LeftHanded = false
  Length = 4
  LengthCustom = 8
  MatchOuter = false
  OffsetAngle = 0
  Placement = pos=(-13.55,22.35,13.5) rot=(0,0,1;0rad)
  Thread = false
  Type = 77
FEATURE [Part::FeaturePython] Screw002  label="M2x8-Screw"  # WARN: FeaturePython — macro-defined, semantics opaque (R4)
  Diameter = 2
  Invert = false
  LeftHanded = false
  Length = 4
  LengthCustom = 8
  MatchOuter = false
  OffsetAngle = 0
  Placement = pos=(-20.45,16.55,13.5) rot=(0,0,1;0rad)
  Thread = false
  Type = 77
FEATURE [Part::FeaturePython] Screw  label="M3x6-Screw"  # WARN: FeaturePython — macro-defined, semantics opaque (R4)
  Diameter = 4
  Invert = false
  LeftHanded = false
  Length = 2
  LengthCustom = 6
  MatchOuter = false
  OffsetAngle = 0
  Placement = pos=(-18,-6.65,3.3) rot=(0,1,0;3.14159rad)
  Thread = false
  Type = 77
FEATURE [Part::FeaturePython] Screw003  label="M3x6-Screw001"  # WARN: FeaturePython — macro-defined, semantics opaque (R4)
  Diameter = 4
  Invert = false
  LeftHanded = false
  Length = 2
  LengthCustom = 6
  MatchOuter = false
  OffsetAngle = 0
  Placement = pos=(6.75,18.1,3.3) rot=(0,1,0;3.14159rad)
  Thread = false
  Type = 77
FEATURE [Sketcher::SketchObject] Sketch024
  ArcFitTolerance = 1e-06
  AttachmentSupport = -> [XY_Plane014]
  FullyConstrained = true
  MakeInternals = false
  MapMode = 5
  sketch-geometry (4):
    g0: LineSegment StartX=0 StartY=-3.3 StartZ=0 EndX=0 EndY=26 EndZ=0
    g1: LineSegment StartX=0 StartY=26 StartZ=0 EndX=-35 EndY=26 EndZ=0
    g2: LineSegment StartX=-35 StartY=26 StartZ=0 EndX=-35 EndY=-3.3 EndZ=0
    g3: LineSegment StartX=-35 StartY=-3.3 StartZ=0 EndX=0 EndY=-3.3 EndZ=0
  constraints (12):
    c: Coincident(g0,g1)
    c: Coincident(g1,g2)
    c: Coincident(g2,g3)
    c: Coincident(g3,g0)
    c: Vertical(g0)
    c: Vertical(g2)
    c: Horizontal(g1)
    c: Horizontal(g3)
    c: Distance(g0,g2) = 35
    c: Distance(g1,g3) = 29.3
    c: PointOnObject(g0,g-2)
    c: Distance(g0,g-1) = 3.3
FEATURE [PartDesign::Pad] Pad015
  Direction = (0,0,1)
  Length = 2
  Length2 = 10
  Midplane = true
  Profile = -> Sketch024
  ReferenceAxis = -> Sketch024 [N_Axis]
  Refine = true
  Suppressed = false
  Type = 0
FEATURE [Sketcher::SketchObject] Sketch025
  ArcFitTolerance = 1e-06
  AttachmentSupport = -> [Pad015]
  FullyConstrained = true
  MakeInternals = false
  MapMode = 5
  Placement = pos=(-35,0,0) rot=(0.57735,-0.57735,-0.57735;2.0944rad)
  sketch-geometry (1):
    g0: Circle CenterX=0 CenterY=0 CenterZ=0 NormalX=0 NormalY=0 NormalZ=1 AngleXU=0 Radius=1
  constraints (2):
    c: Diameter(g0) = 2
    c: Coincident(g0,g-1)
FEATURE [PartDesign::Pad] Pad016
  BaseFeature = -> Pad015
  Direction = (-1,0,0)
  Length = 3
  Length2 = 38
  Profile = -> Sketch025
  ReferenceAxis = -> Sketch025 [N_Axis]
  Refine = true
  Suppressed = false
  Type = 4
FEATURE [PartDesign::Body] Body007  label="Flap1"
  AllowCompound = false
  Group = -> [Sketch024,Pad015,Sketch025,Pad016]
  Origin = -> Origin014
  Placement = pos=(0,0,50.5) rot=(-0.57735,-0.57735,-0.57735;2.0944rad)
  Tip = -> Pad016
FEATURE [PartDesign::FeatureBase] Clone001
  BaseFeature = -> Body007
  Placement = pos=(0,0,50.5) rot=(-0.57735,-0.57735,-0.57735;2.0944rad)
  Suppressed = false
FEATURE [PartDesign::Body] Body008
  AllowCompound = false
  Group = -> [Clone001]
  Origin = -> Origin015
  Placement = pos=(3.75,-11.75,0) rot=(0,0,1;0rad)
  Tip = -> Clone001
FEATURE [PartDesign::FeatureBase] Clone002
  BaseFeature = -> Body007
  Placement = pos=(0,0,50.5) rot=(-0.57735,-0.57735,-0.57735;2.0944rad)
  Suppressed = false
FEATURE [PartDesign::Body] Body009
  AllowCompound = false
  Group = -> [Clone002]
  Origin = -> Origin016
  Placement = pos=(-3.75,-11.75,0) rot=(0,0,1;3.14159rad)
  Tip = -> Clone002
FEATURE [PartDesign::FeatureBase] Clone003
  BaseFeature = -> Body007
  Placement = pos=(0,0,50.5) rot=(-0.57735,-0.57735,-0.57735;2.0944rad)
  Suppressed = false
FEATURE [PartDesign::Body] Body010
  AllowCompound = false
  Group = -> [Clone003]
  Origin = -> Origin017
  Placement = pos=(-10,-7.25,0) rot=(0,0,1;3.26377rad)
  Tip = -> Clone003
FEATURE [PartDesign::FeatureBase] Clone004
  BaseFeature = -> Body007
  Placement = pos=(0,0,50.5) rot=(-0.57735,-0.57735,-0.57735;2.0944rad)
  Suppressed = false
FEATURE [PartDesign::Body] Body011
  AllowCompound = false
  Group = -> [Clone004]
  Origin = -> Origin018
  Placement = pos=(-3.75,11.75,0) rot=(0,0,1;3.14159rad)
  Tip = -> Clone004
FEATURE [PartDesign::FeatureBase] Clone005
  BaseFeature = -> Body007
  Placement = pos=(0,0,50.5) rot=(-0.57735,-0.57735,-0.57735;2.0944rad)
  Suppressed = false
FEATURE [PartDesign::Body] Body012
  AllowCompound = false
  Group = -> [Clone005]
  Origin = -> Origin019
  Placement = pos=(-12.25,1.5e-15,0) rot=(0,0,1;3.47321rad)
  Tip = -> Clone005
FEATURE [PartDesign::FeatureBase] Clone006
  BaseFeature = -> Body007
  Placement = pos=(0,0,50.5) rot=(-0.57735,-0.57735,-0.57735;2.0944rad)
  Suppressed = false
FEATURE [PartDesign::Body] Body013
  AllowCompound = false
  Group = -> [Clone006]
  Origin = -> Origin020
  Placement = pos=(3.75,11.75,0) rot=(0,0,1;2.67035rad)
  Tip = -> Clone006
FEATURE [PartDesign::FeatureBase] Clone007
  BaseFeature = -> Body007
  Placement = pos=(0,0,50.5) rot=(-0.57735,-0.57735,-0.57735;2.0944rad)
  Suppressed = false
FEATURE [PartDesign::Body] Body014
  AllowCompound = false
  Group = -> [Clone007]
  Origin = -> Origin021
  Placement = pos=(10,7.25,0) rot=(0,0,1;1.98968rad)
  Tip = -> Clone007
FEATURE [PartDesign::FeatureBase] Clone008
  BaseFeature = -> Body007
  Placement = pos=(0,0,50.5) rot=(-0.57735,-0.57735,-0.57735;2.0944rad)
  Suppressed = false
FEATURE [PartDesign::Body] Body015
  AllowCompound = false
  Group = -> [Clone008]
  Origin = -> Origin022
  Placement = pos=(12.25,0,0) rot=(0,0,1;1.3439rad)
  Tip = -> Clone008
FEATURE [PartDesign::FeatureBase] Clone009
  BaseFeature = -> Body007
  Placement = pos=(0,0,50.5) rot=(-0.57735,-0.57735,-0.57735;2.0944rad)
  Suppressed = false
FEATURE [PartDesign::Body] Body016
  AllowCompound = false
  Group = -> [Clone009]
  Origin = -> Origin023
  Placement = pos=(10,-7.25,0) rot=(0,0,1;0.750492rad)
  Tip = -> Clone009
FEATURE [PartDesign::FeatureBase] Clone010
  BaseFeature = -> Body007
  Placement = pos=(0,0,50.5) rot=(-0.57735,-0.57735,-0.57735;2.0944rad)
  Suppressed = false
FEATURE [PartDesign::Body] Body017
  AllowCompound = false
  Group = -> [Clone010]
  Origin = -> Origin024
  Placement = pos=(-10,7.25,0) rot=(0,0,1;3.14159rad)
  Tip = -> Clone010
FEATURE [App::Part] Part006  label="Flaps"
  Group = -> [Body007,Body008,Body009,Body010,Body011,Body012,Body013,Body014,Body015,Body016,Body017]
  Origin = -> Origin013
FEATURE [PartDesign::Fillet] Fillet
  Base = -> Revolution [Edge109]
  Radius = 3
  Refine = true
  SupportTransform = false
  Suppressed = false
  UseAllEdges = false
FEATURE [Sketcher::SketchObject] Sketch026
  ArcFitTolerance = 1e-06
  AttachmentSupport = -> [Fillet]
  ExternalGeometry = -> [Fillet]
  FullyConstrained = true
  MakeInternals = false
  MapMode = 5
  Placement = pos=(1.60943e-10,57,-3.5522e-12) rot=(0,0.707107,0.707107;3.14159rad)
  sketch-geometry (3):
    g0: Circle CenterX=-3.95711 CenterY=3.95711 CenterZ=0 NormalX=0 NormalY=0 NormalZ=1 AngleXU=0 Radius=2
    g1: LineSegment [constr] StartX=0 StartY=0 StartZ=0 EndX=-6.5 EndY=6.5 EndZ=0
    g2: GeomPoint [constr] X=-3.25 Y=3.25 Z=0
  constraints (6):
    c: Diameter(g0) = 4
    c: Coincident(g1,g-1)
    c: Symmetric(g-3,g-3,g1)
    c: Symmetric(g1,g1,g2)
    c: PointOnObject(g0,g1)
    c: Distance(g0,g2) = 1
FEATURE [PartDesign::Pocket] Pocket006
  Direction = (-2.8236e-12,-1,6.24e-14)
  Length = 12
  Length2 = 5
  Profile = -> Sketch026
  ReferenceAxis = -> Sketch026 [N_Axis]
  Refine = true
  Suppressed = false
  Type = 0
FEATURE [App::Part] Part  label="Frame"
  Group = -> [Body,Pad,Revolution,Pad010,Chamfer005,Pocket002,Fillet,Pad002,Chamfer,Pad003,Chamfer001,Pad009,Chamfer002,Pocket006,Pad001,Sketch013,Sketch014,Sketch026,Sketch002,Sketch003,Sketch009,Sketch012,Sketch,Sketch001]
  Origin = -> Origin
  Placement = pos=(-48.3,-17.5,4) rot=(0,0,1;0rad)
FEATURE [Part::FeaturePython] Clone011  label="Frame001"  # Draft clone (typed FeaturePython)
  AttacherType = Attacher::AttachEngine3D
  Fuse = false
  Objects = -> [Part]
  Placement = pos=(-48.3,-17.5,104) rot=(0,0,1;0rad)
  Scale = (1,1,-1)
FEATURE [Part::FeaturePython] Clone012  label="Drum001"  # Draft clone (typed FeaturePython)
  AttacherType = Attacher::AttachEngine3D
  Fuse = false
  Objects = -> [Part004]
  Placement = pos=(0,0,57) rot=(0,0,1;0rad)
  Scale = (1,1,-1)
FEATURE [Part::FeaturePython] Clone013  label="Flaps001"  # Draft clone (typed FeaturePython)
  AttacherType = Attacher::AttachEngine3D
  Fuse = false
  Objects = -> [Part006]
  Placement = pos=(0,0,42) rot=(0,0,1;0rad)
  Scale = (1,1,1)
FEATURE [Sketcher::SketchObject] Sketch027
  ArcFitTolerance = 1e-06
  AttachmentSupport = -> [YZ_Plane026]
  FullyConstrained = true
  MakeInternals = false
  MapMode = 5
  Placement = pos=(0,0,0) rot=(0.57735,0.57735,0.57735;2.0944rad)
  sketch-geometry (6):
    g0: LineSegment StartX=0 StartY=0 StartZ=0 EndX=0 EndY=7.75 EndZ=0
    g1: LineSegment StartX=0 StartY=7.75 StartZ=0 EndX=4.8 EndY=7.75 EndZ=0
    g2: LineSegment StartX=4.8 StartY=7.75 StartZ=0 EndX=4.8 EndY=2 EndZ=0
    g3: LineSegment StartX=4.8 StartY=2 StartZ=0 EndX=10 EndY=2 EndZ=0
    g4: LineSegment StartX=10 StartY=2 StartZ=0 EndX=10 EndY=0 EndZ=0
    g5: LineSegment StartX=10 StartY=0 StartZ=0 EndX=0 EndY=0 EndZ=0
  constraints (17):
    c: Coincident(g0,g-1)
    c: PointOnObject(g0,g-2)
    c: Coincident(g1,g0)
    c: Horizontal(g1)
    c: Vertical(g2)
    c: Coincident(g3,g2)
    c: Horizontal(g3)
    c: PointOnObject(g4,g-1)
    c: Vertical(g4)
    c: Coincident(g5,g0)
    c: Distance(g1,g1) = 4.8
    c: Coincident(g2,g1)
    c: Coincident(g3,g4)
    c: Coincident(g5,g4)
    c: DistanceY(g4,g4) = 2
    c: DistanceX(g5,g5) = 10
    c: DistanceY(g2,g2) = 5.75
FEATURE [PartDesign::Revolution] Revolution002
  Angle = 360
  Angle2 = 60
  Axis = (0,0,1)
  Base = (0,0,0)
  Placement = pos=(0,0,0) rot=(1,1,1;2.0944rad)
  Profile = -> Sketch027
  ReferenceAxis = -> Sketch027 [V_Axis]
  Reversed = true
  Suppressed = false
  Type = 0
FEATURE [Sketcher::SketchObject] Sketch028
  ArcFitTolerance = 1e-06
  AttachmentSupport = -> [Revolution002]
  FullyConstrained = true
  MakeInternals = false
  MapMode = 5
  Placement = pos=(-1.7e-15,0,7.75) rot=(0,0,-1;1.5708rad)
  sketch-geometry (5):
    g0: LineSegment StartX=-1.5 StartY=-2.5 StartZ=0 EndX=1.5 EndY=-2.5 EndZ=0
    g1: LineSegment StartX=1.5 StartY=-2.5 StartZ=0 EndX=1.5 EndY=2.5 EndZ=0
    g2: LineSegment StartX=1.5 StartY=2.5 StartZ=0 EndX=-1.5 EndY=2.5 EndZ=0
    g3: LineSegment StartX=-1.5 StartY=2.5 StartZ=0 EndX=-1.5 EndY=-2.5 EndZ=0
    g4: GeomPoint [constr] X=0 Y=0 Z=0
  constraints (12):
    c: Coincident(g0,g1)
    c: Coincident(g1,g2)
    c: Coincident(g2,g3)
    c: Coincident(g3,g0)
    c: Horizontal(g0)
    c: Horizontal(g2)
    c: Vertical(g1)
    c: Vertical(g3)
    c: Symmetric(g2,g0,g4)
    c: Distance(g1,g3) = 3
    c: Distance(g0,g2) = 5
    c: Coincident(g4,g-1)
FEATURE [PartDesign::Pad] Pad017
  BaseFeature = -> Revolution002
  Direction = (0,0,1)
  Length = 5
  Length2 = 10
  Placement = pos=(0,0,0) rot=(1,1,1;2.0944rad)
  Profile = -> Sketch028
  ReferenceAxis = -> Sketch028 [N_Axis]
  Suppressed = false
  Type = 0
FEATURE [PartDesign::Body] Body018
  AllowCompound = false
  Group = -> [Sketch027,Revolution002,Sketch028,Pad017]
  Origin = -> Origin026
  Tip = -> Pad017
FEATURE [App::Part] Part007  label="motor_dummy_axle"
  Group = -> [Body018]
  Origin = -> Origin025
  Placement = pos=(0,0,2) rot=(0,0,1;0rad)
FEATURE [Sketcher::SketchObject] Sketch029
  ArcFitTolerance = 1e-06
  AttachmentSupport = -> [XZ_Plane028]
  FullyConstrained = true
  MakeInternals = false
  MapMode = 5
  Placement = pos=(0,0,0) rot=(1,0,0;1.5708rad)
  sketch-geometry (13):
    g0: LineSegment StartX=-48.3 StartY=-21 StartZ=0 EndX=61.7 EndY=-21 EndZ=0
    g1: LineSegment StartX=61.7 StartY=-21 StartZ=0 EndX=61.7 EndY=129 EndZ=0
    g2: LineSegment StartX=61.7 StartY=129 StartZ=0 EndX=-48.3 EndY=129 EndZ=0
    g3: LineSegment StartX=-48.3 StartY=129 StartZ=0 EndX=-48.3 EndY=-21 EndZ=0
    g4: GeomPoint X=-48.3 Y=54 Z=0
    g5: Circle CenterX=-44.3 CenterY=100.2 CenterZ=0 NormalX=0 NormalY=0 NormalZ=1 AngleXU=0 Radius=2
    g6: Circle CenterX=-44.3 CenterY=7.8 CenterZ=0 NormalX=0 NormalY=0 NormalZ=1 AngleXU=0 Radius=2
    g7: LineSegment [constr] StartX=-44.3 StartY=7.8 StartZ=0 EndX=-44.3 EndY=100.2 EndZ=0
    g8: GeomPoint [constr] X=-44.3 Y=54 Z=0
    g9: Circle CenterX=56.7 CenterY=98 CenterZ=0 NormalX=0 NormalY=0 NormalZ=1 AngleXU=0 Radius=0.975
    g10: Circle CenterX=46.5 CenterY=120 CenterZ=0 NormalX=0 NormalY=0 NormalZ=1 AngleXU=0 Radius=0.975
    g11: Circle CenterX=-38.3 CenterY=74 CenterZ=0 NormalX=0 NormalY=0 NormalZ=1 AngleXU=0 Radius=1.5
    g12: Circle CenterX=1.7 CenterY=34 CenterZ=0 NormalX=0 NormalY=0 NormalZ=1 AngleXU=0 Radius=1.5
  constraints (34):
    c: Coincident(g0,g1)
    c: Coincident(g1,g2)
    c: Coincident(g2,g3)
    c: Coincident(g3,g0)
    c: Horizontal(g0)
    c: Horizontal(g2)
    c: Vertical(g1)
    c: Vertical(g3)
    c: DistanceY(g1,g1) = 150
    c: Symmetric(g3,g3,g4)
    c: DistanceX(g0,g0) = 110
    c: Distance(g3,g-2) = 48.3
    c: DistanceY(g-1,g4) = 54
    c: Diameter(g5) = 4
    c: Coincident(g7,g6)
    c: Coincident(g7,g5)
    c: Vertical(g7)
    c: Symmetric(g7,g7,g8)
    c: Horizontal(g8,g4)
    c: Equal(g5,g6)
    c: Distance(g3,g7) = 4
    c: DistanceY(g8,g5) = 46.2
    c: Diameter(g9) = 1.95
    c: Diameter(g10) = 1.95
    c: DistanceY(g9,g10) = 22
    c: DistanceX(g10,g9) = 10.2
    c: Distance(g9,g1) = 5
    c: Distance(g9,g2) = 31
    c: Diameter(g11) = 3
    c: Diameter(g12) = 3
    c: DistanceX(g11,g12) = 40
    c: DistanceY(g12,g11) = 40
    c: Distance(g11,g3) = 10
    c: DistanceY(g4,g11) = 20
FEATURE [PartDesign::Pad] Pad018
  Direction = (0,-1,2e-16)
  Length = 3
  Length2 = 10
  Placement = pos=(0,0,0) rot=(1,0,0;1.5708rad)
  Profile = -> Sketch029
  ReferenceAxis = -> Sketch029 [N_Axis]
  Suppressed = false
  Type = 0
FEATURE [Sketcher::SketchObject] Sketch030
  ArcFitTolerance = 1e-06
  AttachmentSupport = -> [Pad018]
  ExternalGeometry = -> [Pad018]
  FullyConstrained = true
  MakeInternals = false
  MapMode = 5
  Placement = pos=(0,-3,0) rot=(1,0,0;1.5708rad)
  sketch-geometry (18):
    g0: LineSegment StartX=61.7 StartY=129 StartZ=0 EndX=-48.3 EndY=129 EndZ=0
    g1: LineSegment StartX=-48.3 StartY=129 StartZ=0 EndX=-48.3 EndY=105 EndZ=0
    g2: LineSegment StartX=-48.3 StartY=105 StartZ=0 EndX=-45.3 EndY=105 EndZ=0
    g3: LineSegment StartX=-45.3 StartY=105 StartZ=0 EndX=-45.3 EndY=126 EndZ=0
    g4: LineSegment StartX=-45.3 StartY=126 StartZ=0 EndX=41.7 EndY=126 EndZ=0
    g5: LineSegment StartX=41.7 StartY=126 StartZ=0 EndX=41.7 EndY=-18 EndZ=0
    g6: LineSegment StartX=41.7 StartY=-18 StartZ=0 EndX=-45.3 EndY=-18 EndZ=0
    g7: LineSegment StartX=-45.3 StartY=-18 StartZ=0 EndX=-45.3 EndY=3 EndZ=0
    g8: LineSegment StartX=-45.3 StartY=3 StartZ=0 EndX=-48.3 EndY=3 EndZ=0
    g9: LineSegment StartX=-48.3 StartY=3 StartZ=0 EndX=-48.3 EndY=-21 EndZ=0
    g10: LineSegment StartX=-48.3 StartY=-21 StartZ=0 EndX=61.7 EndY=-21 EndZ=0
    g11: LineSegment StartX=61.7 StartY=129 StartZ=0 EndX=61.7 EndY=126 EndZ=0
    g12: LineSegment StartX=61.7 StartY=126 StartZ=0 EndX=44.7 EndY=126 EndZ=0
    g13: LineSegment StartX=44.7 StartY=126 StartZ=0 EndX=44.7 EndY=-18 EndZ=0
    g14: LineSegment StartX=44.7 StartY=-18 StartZ=0 EndX=61.7 EndY=-18 EndZ=0
    g15: LineSegment StartX=61.7 StartY=-18 StartZ=0 EndX=61.7 EndY=-21 EndZ=0
    g16: LineSegment [constr] StartX=41.7 StartY=126 StartZ=0 EndX=44.7 EndY=126 EndZ=0
    g17: LineSegment [constr] StartX=41.7 StartY=126 StartZ=0 EndX=41.7 EndY=129 EndZ=0
  constraints (49):
    c: Coincident(g-4,g0)
    c: Coincident(g0,g-3)
    c: Coincident(g0,g1)
    c: Vertical(g1)
    c: Coincident(g1,g2)
    c: Horizontal(g2)
    c: Coincident(g2,g3)
    c: Vertical(g3)
    c: Coincident(g3,g4)
    c: Horizontal(g4)
    c: Coincident(g4,g5)
    c: Vertical(g5)
    c: Coincident(g5,g6)
    c: Horizontal(g6)
    c: Coincident(g6,g7)
    c: Vertical(g7)
    c: Coincident(g7,g8)
    c: Horizontal(g8)
    c: Coincident(g8,g9)
    c: Coincident(g9,g-5)
    c: Vertical(g9)
    c: Coincident(g9,g10)
    c: Coincident(g10,g-5)
    c: Coincident(g0,g11)
    c: PointOnObject(g11,g-4)
    c: Coincident(g11,g12)
    c: Horizontal(g12)
    c: Coincident(g12,g13)
    c: Vertical(g13)
    c: Coincident(g13,g14)
    c: PointOnObject(g14,g-4)
    c: Horizontal(g14)
    c: Coincident(g14,g15)
    c: Coincident(g15,g10)
    c: Horizontal(g5,g13)
    c: Vertical(g2,g7)
    c: Horizontal(g4,g12)
    c: Coincident(g16,g4)
    c: Coincident(g16,g12)
    c: Coincident(g17,g4)
    c: PointOnObject(g17,g0)
    c: Vertical(g17)
    c: Equal(g9,g1)
    c: Equal(g2,g16)
    c: Equal(g16,g17)
    c: Equal(g15,g8)
    c: DistanceY(g9,g9) = 24
    c: Distance(g8,g8) = 3
    c: DistanceX(g9,g5) = 90
FEATURE [PartDesign::Pad] Pad019
  BaseFeature = -> Pad018
  Direction = (0,-1,2e-16)
  Length = 57
  Length2 = 10
  Placement = pos=(0,0,0) rot=(1,0,0;1.5708rad)
  Profile = -> Sketch030
  ReferenceAxis = -> Sketch030 [N_Axis]
  Suppressed = false
  Type = 0
FEATURE [Part::Feature] Part__Feature  label="Flat connector_001"
  shape: bbox 16.29 x 6.3 x 1.627 mm, 23 faces (baked)
FEATURE [Part::Feature] Part__Feature001  label="Flat connector_002"
  Placement = pos=(0,-10.3,21.6) rot=(1,0,0;3.14159rad)
  shape: bbox 16.29 x 6.3 x 1.627 mm, 23 faces (baked)
FEATURE [Part::Feature] Part__Feature002  label="Flat connector_005"
  shape: bbox 19.04 x 7.3 x 7.993 mm, 25 faces (baked)
FEATURE [Part::Feature] Part__Feature003  label="Button"
  shape: bbox 3 x 3.9 x 2.5 mm, 6 faces (baked)
FEATURE [Part::Feature] Part__Feature004  label="Case blue"
  shape: bbox 27.8 x 3.1 x 15.8 mm, 219 faces (baked)
FEATURE [Part::Feature] Part__Feature005  label="SOLID"
  shape: bbox 27.8 x 10.3 x 15.8 mm, 140 faces (baked)
FEATURE [Part::Feature] Part__Feature006  label="SOLID001"
  shape: bbox 1.84 x 0.171 x 1.84 mm, 2 faces (baked)
FEATURE [Part::Feature] Part__Feature007  label="SOLID002"
  shape: bbox 1.26 x 1 x 1.26 mm, 4 faces (baked)
FEATURE [Part::Feature] Part__Feature008  label="SOLID003"
  shape: bbox 0.7841 x 0.2025 x 0.7841 mm, 3 faces (baked)
FEATURE [Part::Feature] Part__Feature009  label="SOLID004"
  shape: bbox 0.7841 x 0.2025 x 0.7841 mm, 3 faces (baked)
FEATURE [Part::Feature] Part__Feature010  label="SOLID005"
  shape: bbox 0.7841 x 0.2025 x 0.7841 mm, 3 faces (baked)
FEATURE [Part::Feature] Part__Feature011  label="SOLID006"
  shape: bbox 0.7841 x 0.2025 x 0.7841 mm, 3 faces (baked)
FEATURE [Part::Feature] Part__Feature012  label="SOLID007"
  shape: bbox 0.7841 x 0.2025 x 0.7841 mm, 3 faces (baked)
FEATURE [Part::Feature] Part__Feature013  label="SOLID008"
  shape: bbox 0.7841 x 0.2025 x 0.7841 mm, 3 faces (baked)
FEATURE [Part::Feature] Part__Feature014  label="SOLID009"
  shape: bbox 0.7841 x 0.2025 x 0.7841 mm, 3 faces (baked)
FEATURE [Part::Feature] Part__Feature015  label="SOLID010"
  shape: bbox 0.7841 x 0.2025 x 0.7841 mm, 3 faces (baked)
FEATURE [Part::Feature] Part__Feature016  label="SOLID011"
  shape: bbox 0.7841 x 0.2025 x 0.7841 mm, 3 faces (baked)
FEATURE [Part::Feature] Part__Feature017  label="SOLID012"
  shape: bbox 0.7841 x 0.2025 x 0.7841 mm, 3 faces (baked)
FEATURE [Part::Feature] Part__Feature018  label="SOLID013"
  shape: bbox 0.7841 x 0.2025 x 0.7841 mm, 3 faces (baked)
FEATURE [Part::Feature] Part__Feature019  label="SOLID014"
  shape: bbox 0.7841 x 0.2025 x 0.7841 mm, 3 faces (baked)
FEATURE [App::Part] Case_black  label="Case black"
  Group = -> [Part__Feature005,Part__Feature006,Part__Feature007,Part__Feature008,Part__Feature009,Part__Feature010,Part__Feature011,Part__Feature012,Part__Feature013,Part__Feature014,Part__Feature015,Part__Feature016,Part__Feature017,Part__Feature018,Part__Feature019]
  Origin = -> Origin029
FEATURE [App::Part] Crouzet_83_161_118
  Group = -> [Part__Feature,Part__Feature001,Part__Feature002,Part__Feature003,Part__Feature004,Case_black]
  Origin = -> Origin030
  Placement = pos=(43.7573,39.2694,123.307) rot=(0,-1,0;4.71239rad)
FEATURE [Sketcher::SketchObject] Sketch031
  ArcFitTolerance = 1e-06
  AttachmentSupport = -> [Pad019]
  ExternalGeometry = -> [Pad019]
  FullyConstrained = false
  MakeInternals = false
  MapMode = 5
  Placement = pos=(0,-60,1.32e-14) rot=(1,0,0;1.5708rad)
  sketch-geometry (27):
    g0: LineSegment StartX=-48.3 StartY=-21 StartZ=0 EndX=-48.3 EndY=-6 EndZ=0
    g1: LineSegment StartX=-48.3 StartY=-6 StartZ=0 EndX=-33.3 EndY=-21 EndZ=0
    g2: LineSegment StartX=-33.3 StartY=-21 StartZ=0 EndX=-48.3 EndY=-21 EndZ=0
    g3: LineSegment [constr] StartX=-48.3 StartY=-21 StartZ=0 EndX=-40.8 EndY=-13.5 EndZ=0
    g4: LineSegment [constr] StartX=-48.3 StartY=129 StartZ=0 EndX=-48.3 EndY=-21 EndZ=0
    g5: GeomPoint [constr] X=-48.3 Y=54 Z=0
    g6: LineSegment [constr] StartX=41.7 StartY=126 StartZ=0 EndX=-48.3 EndY=126 EndZ=0
    g7: GeomPoint [constr] X=-3.3 Y=126 Z=0
    g8: LineSegment [constr] StartX=-48.3 StartY=54 StartZ=0 EndX=41.7 EndY=54 EndZ=0
    g9: Circle CenterX=-43.3 CenterY=-16 CenterZ=0 NormalX=0 NormalY=0 NormalZ=1 AngleXU=0 Radius=1.525
    g10: LineSegment StartX=-48.3 StartY=129 StartZ=0 EndX=-48.3 EndY=114 EndZ=0
    g11: LineSegment StartX=-48.3 StartY=114 StartZ=0 EndX=-33.3 EndY=129 EndZ=0
    g12: LineSegment StartX=-33.3 StartY=129 StartZ=0 EndX=-48.3 EndY=129 EndZ=0
    g13: LineSegment [constr] StartX=-48.3 StartY=129 StartZ=0 EndX=-40.8 EndY=121.5 EndZ=0
    g14: Circle CenterX=-43.3 CenterY=124 CenterZ=0 NormalX=0 NormalY=0 NormalZ=1 AngleXU=0 Radius=1.525
    g15: LineSegment [constr] StartX=-3.3 StartY=126 StartZ=0 EndX=-3.3 EndY=54 EndZ=0
    g16: LineSegment StartX=41.7 StartY=-21 StartZ=0 EndX=41.7 EndY=-6 EndZ=0
    g17: LineSegment StartX=41.7 StartY=-6 StartZ=0 EndX=26.7 EndY=-21 EndZ=0
    g18: LineSegment StartX=26.7 StartY=-21 StartZ=0 EndX=41.7 EndY=-21 EndZ=0
    g19: LineSegment [constr] StartX=41.7 StartY=-21 StartZ=0 EndX=34.2 EndY=-13.5 EndZ=0
    g20: GeomPoint [constr] X=41.7 Y=54 Z=0
    g21: Circle CenterX=36.7 CenterY=-16 CenterZ=0 NormalX=0 NormalY=0 NormalZ=1 AngleXU=0 Radius=1.525
    g22: LineSegment StartX=41.7 StartY=129 StartZ=0 EndX=41.7 EndY=114 EndZ=0
    g23: LineSegment StartX=41.7 StartY=114 StartZ=0 EndX=26.7 EndY=129 EndZ=0
    g24: LineSegment StartX=26.7 StartY=129 StartZ=0 EndX=41.7 EndY=129 EndZ=0
    g25: LineSegment [constr] StartX=41.7 StartY=129 StartZ=0 EndX=34.2 EndY=121.5 EndZ=0
    g26: Circle CenterX=36.7 CenterY=124 CenterZ=0 NormalX=0 NormalY=0 NormalZ=1 AngleXU=0 Radius=1.525
  constraints (54):
    c: Coincident(g0,g-3)
    c: Vertical(g0)
    c: Coincident(g0,g1)
    c: Coincident(g1,g2)
    c: Coincident(g2,g0)
    c: Horizontal(g2)
    c: Coincident(g3,g0)
    c: Symmetric(g1,g1,g3)
    c: DistanceY(g0,g0) = 15
    c: Equal(g2,g0)
    c: Coincident(g4,g-4)
    c: Coincident(g4,g0)
    c: Symmetric(g4,g4,g5)
    c: Coincident(g6,g-5)
    c: PointOnObject(g6,g4)
    c: Horizontal(g6)
    c: Symmetric(g6,g6,g7)
    c: Coincident(g8,g5)
    c: Horizontal(g8)
    c: Vertical(g8,g6)
    c: Diameter(g9) = 3.05
    c: PointOnObject(g9,g3)
    c: Distance(g9,g0) = 5
    c: Vertical(g10)
    c: Coincident(g10,g11)
    c: Coincident(g11,g12)
    c: Coincident(g12,g10)
    c: Horizontal(g12)
    c: Coincident(g13,g10)
    c: Symmetric(g11,g11,g13)
    c: Equal(g12,g10)
    c: Diameter(g14) = 3.05
    c: PointOnObject(g14,g13)
    c: Distance(g14,g10) = 5
    c: Coincident(g15,g7)
    c: Symmetric(g8,g8,g15)
    c: Coincident(g16,g17)
    c: Coincident(g17,g18)
    c: Coincident(g18,g16)
    c: Coincident(g19,g16)
    c: Symmetric(g17,g17,g19)
    c: Equal(g18,g16)
    c: Diameter(g21) = 3.05
    c: PointOnObject(g21,g19)
    c: Distance(g21,g16) = 5
    c: Coincident(g22,g23)
    c: Coincident(g23,g24)
    c: Coincident(g24,g22)
    c: Coincident(g25,g22)
    c: Symmetric(g23,g23,g25)
    c: Equal(g24,g22)
    c: Diameter(g26) = 3.05
    c: PointOnObject(g26,g25)
    c: Distance(g26,g22) = 5
FEATURE [PartDesign::Pad] Pad020
  BaseFeature = -> Pad019
  Direction = (0,-1,2e-16)
  Length = 5
  Length2 = 10
  Placement = pos=(0,0,0) rot=(1,0,0;1.5708rad)
  Profile = -> Sketch031
  ReferenceAxis = -> Sketch031 [N_Axis]
  Reversed = true
  Suppressed = false
  Type = 0
FEATURE [Sketcher::SketchObject] Sketch032
  ArcFitTolerance = 1e-06
  AttachmentSupport = -> [Pad020]
  ExternalGeometry = -> [Pad020]
  FullyConstrained = true
  MakeInternals = false
  MapMode = 5
  Placement = pos=(44.7,0,0) rot=(0.707107,0,0.707107;3.14159rad)
  sketch-geometry (6):
    g0: LineSegment StartX=126 StartY=3 StartZ=0 EndX=126 EndY=14 EndZ=0
    g1: LineSegment StartX=126 StartY=14 StartZ=0 EndX=66 EndY=14 EndZ=0
    g2: LineSegment StartX=61 StartY=9 StartZ=0 EndX=61 EndY=3 EndZ=0
    g3: LineSegment StartX=61 StartY=3 StartZ=0 EndX=126 EndY=3 EndZ=0
    g4: ArcOfCircle CenterX=66 CenterY=9 CenterZ=0 NormalX=0 NormalY=0 NormalZ=1 AngleXU=0 Radius=5 StartAngle=1.5708 EndAngle=3.14159
    g5: GeomPoint [constr] X=61 Y=14 Z=0
  constraints (15):
    c: Coincident(g0,g1)
    c: Coincident(g2,g3)
    c: Coincident(g3,g0)
    c: Vertical(g0)
    c: Vertical(g2)
    c: Horizontal(g1)
    c: Horizontal(g3)
    c: Distance(g0,g2) = 65
    c: Distance(g1,g3) = 11
    c: Coincident(g0,g-3)
    c: PointOnObject(g5,g1)
    c: PointOnObject(g5,g2)
    c: Tangent(g1,g4) = -1.5708
    c: Tangent(g2,g4) = -1.5708
    c: Radius(g4) = 5
FEATURE [PartDesign::Pocket] Pocket007
  BaseFeature = -> Pad020
  Direction = (-1,0,2e-16)
  Length = 5
  Length2 = 5
  Placement = pos=(0,0,0) rot=(1,0,0;1.5708rad)
  Profile = -> Sketch032
  ReferenceAxis = -> Sketch032 [N_Axis]
  Suppressed = false
  Type = 2
FEATURE [PartDesign::Body] Body019  label="Back"
  AllowCompound = false
  Group = -> [Sketch029,Pad018,Sketch030,Pad019,Sketch031,Pad020,Sketch032,Pocket007]
  Origin = -> Origin028
  Tip = -> Pocket007
FEATURE [Sketcher::SketchObject] Sketch033
  ArcFitTolerance = 1e-06
  AttachmentSupport = -> [Pocket007]
  FullyConstrained = false
  MakeInternals = false
  MapMode = 5
  Placement = pos=(0,-60,1.32e-14) rot=(1,0,0;1.5708rad)
  sketch-geometry (23):
    g0: LineSegment StartX=-48.3 StartY=129 StartZ=0 EndX=-48.3 EndY=104.209 EndZ=0
    g1: LineSegment StartX=-48.3 StartY=-21 StartZ=0 EndX=61.7 EndY=-21 EndZ=0
    g2: LineSegment StartX=61.7 StartY=-21 StartZ=0 EndX=61.7 EndY=37.5 EndZ=0
    g3: LineSegment StartX=61.7 StartY=129 StartZ=0 EndX=-48.3 EndY=129 EndZ=0
    g4: LineSegment StartX=-38.3 StartY=11.5 StartZ=0 EndX=27.7 EndY=11.5 EndZ=0
    g5: LineSegment StartX=27.7 StartY=11.5 StartZ=0 EndX=27.7 EndY=96.5 EndZ=0
    g6: LineSegment StartX=27.7 StartY=96.5 StartZ=0 EndX=-38.3 EndY=96.5 EndZ=0
    g7: Circle CenterX=-43.3 CenterY=-16 CenterZ=0 NormalX=0 NormalY=0 NormalZ=1 AngleXU=0 Radius=1.8
    g8: Circle CenterX=36.7 CenterY=-16 CenterZ=0 NormalX=0 NormalY=0 NormalZ=1 AngleXU=0 Radius=1.8
    g9: Circle CenterX=36.7 CenterY=124 CenterZ=0 NormalX=0 NormalY=0 NormalZ=1 AngleXU=0 Radius=1.8
    g10: Circle CenterX=-43.3 CenterY=124 CenterZ=0 NormalX=0 NormalY=0 NormalZ=1 AngleXU=0 Radius=1.8
    g11: GeomPoint X=61.7 Y=54 Z=0
    g12: GeomPoint X=27.7 Y=54 Z=0
    g13: LineSegment StartX=60.7 StartY=69.5 StartZ=0 EndX=58.7 EndY=69.5 EndZ=0
    g14: LineSegment StartX=58.7 StartY=69.5 StartZ=0 EndX=58.7 EndY=38.5 EndZ=0
    g15: LineSegment StartX=58.7 StartY=38.5 StartZ=0 EndX=60.7 EndY=38.5 EndZ=0
    g16: GeomPoint X=58.7 Y=54 Z=0
    g17: LineSegment StartX=61.7 StartY=70.5 StartZ=0 EndX=61.7 EndY=129 EndZ=0
    g18: LineSegment StartX=-48.3 StartY=4 StartZ=0 EndX=-48.3 EndY=-21 EndZ=0
    g19: LineSegment StartX=-48.3 StartY=4 StartZ=0 EndX=-48.3 EndY=104.209 EndZ=0
    g20: LineSegment StartX=-38.3 StartY=96.5 StartZ=0 EndX=-38.3 EndY=11.5 EndZ=0
    g21: ArcOfCircle CenterX=60.7 CenterY=70.5 CenterZ=0 NormalX=0 NormalY=0 NormalZ=1 AngleXU=0 Radius=1 StartAngle=4.71239 EndAngle=6.28319
    g22: ArcOfCircle CenterX=60.7 CenterY=37.5 CenterZ=0 NormalX=0 NormalY=0 NormalZ=1 AngleXU=0 Radius=1 StartAngle=2.1e-15 EndAngle=1.5708
  constraints (59):
    c: Coincident(g18,g1)
    c: Coincident(g1,g2)
    c: Coincident(g17,g3)
    c: Coincident(g3,g0)
    c: Vertical(g0)
    c: Vertical(g2)
    c: Horizontal(g1)
    c: Horizontal(g3)
    c: DistanceX(g1,g1) = 110
    c: DistanceY(g2,g17) = 150
    c: Coincident(g4,g5)
    c: Coincident(g5,g6)
    c: Vertical(g5)
    c: Horizontal(g4)
    c: Horizontal(g6)
    c: DistanceY(g5,g5) = 85
    c: Distance(g0,g-2) = 48.3
    c: Distance(g-1,g1) = 21
    c: Equal(g10,g9)
    c: Equal(g9,g7)
    c: Equal(g7,g8)
    c: Diameter(g7) = 3.6
    c: Horizontal(g7,g8)
    c: Vertical(g8,g9)
    c: Horizontal(g9,g10)
    c: Vertical(g10,g7)
    c: Distance(g7,g0) = 5
    c: Distance(g7,g1) = 5
    c: Distance(g10,g3) = 5
    c: Distance(g9,g0) = 85
    c: Symmetric(g2,g17,g11)
    c: Symmetric(g5,g5,g12)
    c: Horizontal(g12,g11)
    c: Coincident(g13,g14)
    c: Coincident(g14,g15)
    c: Horizontal(g13)
    c: Horizontal(g15)
    c: Vertical(g14)
    c: Symmetric(g14,g14,g16)
    c: Horizontal(g16,g11)
    c: DistanceY(g14,g14) = 31
    c: Coincident(g19,g0)
    c: Vertical(g19)
    c: Vertical(g20)
    c: Distance(g20,g19) = 10
    c: Coincident(g4,g20)
    c: Coincident(g6,g20)
    c: Tangent(g13,g21) = 1.5708
    c: Tangent(g17,g21) = -1.5708
    c: Tangent(g15,g22) = 1.5708
    c: Tangent(g2,g22) = -1.5708
    c: Equal(g22,g21)
    c: Radius(g21) = 1
    c: Vertical(g17)
    c: Vertical(g17,g2)
    c: Distance(g2,g14) = 3
    c: Vertical(g18)
    c: Coincident(g18,g19)
    c: DistanceX(g6,g6) = 66
FEATURE [PartDesign::Pad] Pad021
  Direction = (0,-1,2e-16)
  Length = 3
  Length2 = 10
  Placement = pos=(0,0,0) rot=(1,0,0;1.5708rad)
  Profile = -> Sketch033
  ReferenceAxis = -> Sketch033 [N_Axis]
  Suppressed = false
  Type = 0
FEATURE [Sketcher::SketchObject] Sketch034
  ArcFitTolerance = 1e-06
  AttachmentSupport = -> [Pad021]
  ExternalGeometry = -> [Pad021]
  FullyConstrained = true
  MakeInternals = false
  MapMode = 5
  Placement = pos=(0,5.68e-14,129) rot=(0,0,1;3.14159rad)
  sketch-geometry (1):
    g0: Circle CenterX=-58.7 CenterY=6 CenterZ=0 NormalX=0 NormalY=0 NormalZ=1 AngleXU=0 Radius=1.5
  constraints (3):
    c: Diameter(g0) = 3
    c: DistanceX(g-3,g0) = 3
    c: DistanceY(g-3,g0) = 3
FEATURE [PartDesign::Pocket] Pocket008
  BaseFeature = -> Pad021
  Direction = (0,0,-1)
  Length = 5
  Length2 = 5
  Placement = pos=(0,0,0) rot=(1,0,0;1.5708rad)
  Profile = -> Sketch034
  ReferenceAxis = -> Sketch034 [N_Axis]
  Suppressed = false
  Type = 1
FEATURE [Part::Part2DObjectPython] ShapeString  # Draft 2D object (typed FeaturePython)
  FontFile = <path>
  Fuse = false
  Justification = 6
  JustificationReference = 0
  KeepLeftMargin = false
  MakeFace = true
  ObliqueAngle = 0
  Placement = pos=(43.904,-63,126.197) rot=(-0.57735,-0.57735,0.57735;4.18879rad)
  ScaleToSize = true
  Size = 11
  String = Days without incident
  Tracking = 0
FEATURE [PartDesign::Pocket] Pocket009
  BaseFeature = -> Pocket008
  Direction = (0,1,-2e-16)
  Length = 0.6
  Length2 = 5
  Placement = pos=(0,0,0) rot=(1,0,0;1.5708rad)
  Profile = -> ShapeString
  ReferenceAxis = -> ShapeString [N_Axis]
  Suppressed = false
  Type = 0
FEATURE [PartDesign::Body] Body020  label="Front"
  AllowCompound = false
  Group = -> [Sketch033,Pad021,Sketch034,Pocket008,ShapeString,Pocket009]
  Origin = -> Origin031
  Tip = -> Pocket009
FEATURE [App::Part] Part008  label="BackCover"
  Group = -> [Body019,Body020]
  Origin = -> Origin027
  Placement = pos=(0,42.45,0) rot=(0,0,1;0rad)
FEATURE [Part::Extrusion] Extrude
  Dir = (0,-1,2e-16)
  DirMode = 2
  FaceMakerClass = Part::FaceMakerBullseye
  FaceMakerMode = 3
  LengthFwd = 0.6
  LengthRev = 0
  Placement = pos=(0,0.6,0) rot=(0,0,1;0rad)
  Solid = false
  Symmetric = false
FEATURE [Sketcher::SketchObject] Sketch035
  ArcFitTolerance = 1e-06
  AttachmentSupport = -> [YZ_Plane033]
  FullyConstrained = false
  MakeInternals = false
  MapMode = 5
  Placement = pos=(0,0,0) rot=(0.57735,0.57735,0.57735;2.0944rad)
  sketch-geometry (15):
    g0: LineSegment StartX=42.45 StartY=129 StartZ=0 EndX=-20.55 EndY=129 EndZ=0
    g1: LineSegment StartX=-20.55 StartY=129 StartZ=0 EndX=-20.55 EndY=69 EndZ=0
    g2: LineSegment StartX=-20.55 StartY=-21 StartZ=0 EndX=42.45 EndY=-21 EndZ=0
    g3: LineSegment StartX=42.45 StartY=-21 StartZ=0 EndX=42.45 EndY=129 EndZ=0
    g4: GeomPoint X=-20.55 Y=54 Z=0
    g5: LineSegment StartX=-20.55 StartY=69 StartZ=0 EndX=-20.75 EndY=69 EndZ=0
    g6: LineSegment StartX=-22.55 StartY=67.2 StartZ=0 EndX=-22.55 EndY=40.8 EndZ=0
    g7: LineSegment StartX=-20.75 StartY=39 StartZ=0 EndX=-20.55 EndY=39 EndZ=0
    g8: GeomPoint X=-20.55 Y=54 Z=0
    g9: GeomPoint X=-20.55 Y=54 Z=0
    g10: ArcOfCircle CenterX=-20.75 CenterY=40.8 CenterZ=0 NormalX=0 NormalY=0 NormalZ=1 AngleXU=0 Radius=1.8 StartAngle=3.14159 EndAngle=4.71239
    g11: GeomPoint [constr] X=-22.55 Y=39 Z=0
    g12: ArcOfCircle CenterX=-20.75 CenterY=67.2 CenterZ=0 NormalX=0 NormalY=0 NormalZ=1 AngleXU=0 Radius=1.8 StartAngle=1.5708 EndAngle=3.14159
    g13: GeomPoint [constr] X=-22.55 Y=69 Z=0
    g14: LineSegment StartX=-20.55 StartY=39 StartZ=0 EndX=-20.55 EndY=-21 EndZ=0
  constraints (33):
    c: Coincident(g0,g1)
    c: Coincident(g14,g2)
    c: Coincident(g2,g3)
    c: Coincident(g3,g0)
    c: Horizontal(g0)
    c: Horizontal(g2)
    c: Vertical(g1)
    c: Vertical(g3)
    c: DistanceX(g2,g2) = 63
    c: DistanceY(g3,g3) = 150
    c: Distance(g0,g-2) = 20.55
    c: DistanceY(g14,g-1) = 21
    c: Symmetric(g1,g14,g4)
    c: Horizontal(g5)
    c: Horizontal(g7)
    c: Vertical(g6)
    c: Distance(g13,g5) = 2
    c: Distance(g5,g7) = 30
    c: Symmetric(g1,g14,g8)
    c: Symmetric(g1,g14,g9)
    c: Symmetric(g7,g5,g4)
    c: PointOnObject(g11,g6)
    c: PointOnObject(g11,g7)
    c: Tangent(g6,g10) = -1.5708
    c: Tangent(g7,g10) = -1.5708
    c: PointOnObject(g13,g5)
    c: PointOnObject(g13,g6)
    c: Tangent(g5,g12) = -1.5708
    c: Tangent(g6,g12) = -1.5708
    c: Equal(g12,g10)
    c: Radius(g10) = 1.8
    c: PointOnObject(g1,g5)
    c: PointOnObject(g14,g7)
FEATURE [PartDesign::Pad] Pad022
  Direction = (1,0,0)
  Length = 5
  Length2 = 10
  Placement = pos=(0,0,0) rot=(1,1,1;2.0944rad)
  Profile = -> Sketch035
  ReferenceAxis = -> Sketch035 [N_Axis]
  Suppressed = false
  Type = 0
FEATURE [Sketcher::SketchObject] Sketch036
  ArcFitTolerance = 1e-06
  AttachmentSupport = -> [Pad022]
  ExternalGeometry = -> [Pad022]
  FullyConstrained = true
  MakeInternals = false
  MapMode = 5
  Placement = pos=(0,0,0) rot=(0.57735,0.57735,-0.57735;4.18879rad)
  sketch-geometry (4):
    g0: LineSegment StartX=39.45 StartY=18 StartZ=0 EndX=-17.55 EndY=18 EndZ=0
    g1: LineSegment StartX=-17.55 StartY=18 StartZ=0 EndX=-17.55 EndY=-126 EndZ=0
    g2: LineSegment StartX=-17.55 StartY=-126 StartZ=0 EndX=39.45 EndY=-126 EndZ=0
    g3: LineSegment StartX=39.45 StartY=-126 StartZ=0 EndX=39.45 EndY=18 EndZ=0
  constraints (12):
    c: Coincident(g0,g1)
    c: Coincident(g1,g2)
    c: Coincident(g2,g3)
    c: Coincident(g3,g0)
    c: Horizontal(g0)
    c: Horizontal(g2)
    c: Vertical(g1)
    c: Vertical(g3)
    c: DistanceX(g-4,g1) = 3
    c: DistanceY(g-4,g1) = 3
    c: DistanceY(g0,g-3) = 3
    c: DistanceX(g0,g-3) = 3
FEATURE [PartDesign::Pocket] Pocket010
  BaseFeature = -> Pad022
  Direction = (1,0,0)
  Length = 3
  Length2 = 5
  Placement = pos=(0,0,0) rot=(1,1,1;2.0944rad)
  Profile = -> Sketch036
  ReferenceAxis = -> Sketch036 [N_Axis]
  Suppressed = false
  Type = 0
FEATURE [Sketcher::SketchObject] Sketch037
  ArcFitTolerance = 1e-06
  AttachmentSupport = -> [Pocket010]
  ExternalGeometry = -> [Pocket010]
  FullyConstrained = true
  MakeInternals = false
  MapMode = 5
  Placement = pos=(0,2.84e-14,129) rot=(0,0,-1;1.5708rad)
  sketch-geometry (6):
    g0: LineSegment StartX=-42.45 StartY=5 StartZ=0 EndX=-42.45 EndY=-1.95e-14 EndZ=0
    g1: LineSegment StartX=-42.45 StartY=-1.95e-14 StartZ=0 EndX=-42.45 EndY=-5 EndZ=0
    g2: ArcOfCircle CenterX=-37.45 CenterY=-5 CenterZ=0 NormalX=0 NormalY=0 NormalZ=1 AngleXU=0 Radius=5 StartAngle=3.14159 EndAngle=5.93412
    g3: LineSegment StartX=-32.7515 StartY=-6.7101 StartZ=0 EndX=-28.4894 EndY=5 EndZ=0
    g4: LineSegment StartX=-28.4894 StartY=5 StartZ=0 EndX=-42.45 EndY=5 EndZ=0
    g5: Circle CenterX=-37.45 CenterY=-5 CenterZ=0 NormalX=0 NormalY=0 NormalZ=1 AngleXU=0 Radius=1.6
  constraints (14):
    c: Coincident(g-3,g0)
    c: Coincident(g0,g-3)
    c: Coincident(g0,g1)
    c: Tangent(g1,g2) = -1.5708
    c: Coincident(g3,g4)
    c: Coincident(g4,g0)
    c: Horizontal(g4)
    c: Diameter(g5) = 3.2
    c: Coincident(g5,g2)
    c: Tangent(g2,g3) = -1.5708
    c: Radius(g2) = 5
    c: Distance(g2,g-1) = 5
    c: Vertical(g1)
    c: Angle(g4,g3) = 1.22173
FEATURE [PartDesign::Pad] Pad023
  BaseFeature = -> Pocket010
  Direction = (0,0,1)
  Length = 3
  Length2 = 10
  Placement = pos=(0,0,0) rot=(1,1,1;2.0944rad)
  Profile = -> Sketch037
  ReferenceAxis = -> Sketch037 [N_Axis]
  Suppressed = false
  Type = 0
FEATURE [PartDesign::LinearPattern] LinearPattern
  BaseFeature = -> Pad023
  Direction = -> Sketch037 [N_Axis]
  Length = 153
  Mode = 0
  Occurrences = 2
  Offset = 153
  Originals = -> [Pad023]
  Placement = pos=(0,0,0) rot=(1,1,1;2.0944rad)
  Reversed = true
  Suppressed = false
  TransformMode = 0
FEATURE [PartDesign::Fillet] Fillet001
  Base = -> LinearPattern [Edge4,Edge41]
  BaseFeature = -> LinearPattern
  Placement = pos=(0,0,0) rot=(1,1,1;2.0944rad)
  Radius = 2.9
  SupportTransform = false
  Suppressed = false
  UseAllEdges = false
FEATURE [PartDesign::Chamfer] Chamfer011
  Angle = 45
  Base = -> Fillet001 [Edge7]
  BaseFeature = -> Fillet001
  ChamferType = 1
  FlipDirection = false
  Placement = pos=(0,0,0) rot=(1,1,1;2.0944rad)
  Size = 2.5
  Size2 = 4
  SupportTransform = false
  Suppressed = false
  UseAllEdges = false
FEATURE [PartDesign::Fillet] Fillet002
  Base = -> Chamfer011 [Edge63,Edge61,Edge64,Edge59]
  BaseFeature = -> Chamfer011
  Placement = pos=(0,0,0) rot=(1,1,1;2.0944rad)
  Radius = 2.9
  SupportTransform = false
  Suppressed = false
  UseAllEdges = false
FEATURE [PartDesign::Hole] Hole001
  BaseFeature = -> Fillet002
  CustomThreadClearance = 0
  Depth = 2
  DepthType = 0
  Diameter = 6
  DrillForDepth = false
  DrillPoint = 0
  DrillPointAngle = 118
  HoleCutCountersinkAngle = 90
  HoleCutCustomValues = false
  HoleCutDepth = 0
  HoleCutDiameter = 6.1
  HoleCutType = 0
  ModelThread = false
  Placement = pos=(0,0,0) rot=(1,1,1;2.0944rad)
  Profile = -> Fillet002 [Edge84]
  Suppressed = false
  Tapered = false
  TaperedAngle = 90
  ThreadClass = 0
  ThreadDepth = 2
  ThreadDepthType = 0
  ThreadDirection = 0
  ThreadFit = 0
  ThreadSize = 0
  ThreadType = 0
  Threaded = false
  UseCustomThreadClearance = false
FEATURE [PartDesign::Hole] Hole002
  BaseFeature = -> Hole001
  CustomThreadClearance = 0
  Depth = 1.5
  DepthType = 0
  Diameter = 6
  DrillForDepth = false
  DrillPoint = 0
  DrillPointAngle = 118
  HoleCutCountersinkAngle = 90
  HoleCutCustomValues = false
  HoleCutDepth = 0
  HoleCutDiameter = 6.1
  HoleCutType = 0
  ModelThread = false
  Placement = pos=(0,0,0) rot=(1,1,1;2.0944rad)
  Profile = -> Hole001 [Edge100]
  Reversed = true
  Suppressed = false
  Tapered = false
  TaperedAngle = 90
  ThreadClass = 0
  ThreadDepth = 1.5
  ThreadDepthType = 0
  ThreadDirection = 0
  ThreadFit = 0
  ThreadSize = 0
  ThreadType = 0
  Threaded = false
  UseCustomThreadClearance = false
FEATURE [Sketcher::SketchObject] Sketch038
  ArcFitTolerance = 1e-06
  AttachmentSupport = -> [Hole002]
  ExternalGeometry = -> [Hole002]
  FullyConstrained = true
  MakeInternals = false
  MapMode = 5
  Placement = pos=(0,0,0) rot=(0.57735,0.57735,-0.57735;4.18879rad)
  sketch-geometry (6):
    g0: LineSegment StartX=-22.55 StartY=-67.2 StartZ=0 EndX=-22.55 EndY=-40.8 EndZ=0
    g1: ArcOfCircle CenterX=-20.75 CenterY=-40.8 CenterZ=0 NormalX=0 NormalY=0 NormalZ=1 AngleXU=0 Radius=1.8 StartAngle=1.5708 EndAngle=3.14159
    g2: LineSegment StartX=-20.75 StartY=-39 StartZ=0 EndX=-17.55 EndY=-39 EndZ=0
    g3: LineSegment StartX=-17.55 StartY=-39 StartZ=0 EndX=-17.55 EndY=-69 EndZ=0
    g4: LineSegment StartX=-17.55 StartY=-69 StartZ=0 EndX=-20.75 EndY=-69 EndZ=0
    g5: ArcOfCircle CenterX=-20.75 CenterY=-67.2 CenterZ=0 NormalX=0 NormalY=0 NormalZ=1 AngleXU=0 Radius=1.8 StartAngle=3.14159 EndAngle=4.71239
  constraints (13):
    c: Tangent(g-4,g0) = 1.5708
    c: Tangent(g0,g1) = 1.5708
    c: Coincident(g1,g-3)
    c: Tangent(g1,g2) = 1.5708
    c: Coincident(g2,g3)
    c: Vertical(g3)
    c: Coincident(g3,g4)
    c: Coincident(g4,g-4)
    c: Horizontal(g4)
    c: Tangent(g4,g5) = 1.5708
    c: Coincident(g5,g0)
    c: PointOnObject(g3,g-5)
    c: Horizontal(g2)
FEATURE [PartDesign::Pad] Pad024
  BaseFeature = -> Hole002
  Direction = (-1,1e-15,-1e-16)
  Length = 3
  Length2 = 10
  Placement = pos=(0,0,0) rot=(1,1,1;2.0944rad)
  Profile = -> Sketch038
  ReferenceAxis = -> Sketch038 [N_Axis]
  Suppressed = false
  Type = 0
FEATURE [PartDesign::Fillet] Fillet003
  Base = -> Pad024 [Edge16,Edge20]
  BaseFeature = -> Pad024
  Placement = pos=(0,0,0) rot=(1,1,1;2.0944rad)
  Radius = 1
  SupportTransform = false
  Suppressed = false
  UseAllEdges = false
FEATURE [Sketcher::SketchObject] Sketch039
  ArcFitTolerance = 1e-06
  AttachmentSupport = -> [Fillet003]
  ExternalGeometry = -> [Fillet003]
  FullyConstrained = false
  MakeInternals = false
  MapMode = 5
  Placement = pos=(3,0,0) rot=(0.57735,0.57735,-0.57735;4.18879rad)
  sketch-geometry (4):
    g0: LineSegment StartX=29.6432 StartY=-113.503 StartZ=0 EndX=29.6432 EndY=-123.1 EndZ=0
    g1: LineSegment StartX=29.6432 StartY=-123.1 StartZ=0 EndX=36.55 EndY=-123.1 EndZ=0
    g2: LineSegment StartX=36.55 StartY=-123.1 StartZ=0 EndX=36.55 EndY=-113.503 EndZ=0
    g3: LineSegment StartX=36.55 StartY=-113.503 StartZ=0 EndX=29.6432 EndY=-113.503 EndZ=0
  constraints (9):
    c: Coincident(g0,g1)
    c: Coincident(g1,g2)
    c: Coincident(g2,g3)
    c: Coincident(g3,g0)
    c: Vertical(g0)
    c: Vertical(g2)
    c: Horizontal(g1)
    c: Horizontal(g3)
    c: Coincident(g1,g-3)
FEATURE [PartDesign::Pad] Pad025
  BaseFeature = -> Fillet003
  Direction = (-1,1e-15,-1e-16)
  Length = 5
  Length2 = 10
  Placement = pos=(0,0,0) rot=(1,1,1;2.0944rad)
  Profile = -> Sketch039
  ReferenceAxis = -> Sketch039 [N_Axis]
  Suppressed = false
  TaperAngle = -20
  Type = 0
FEATURE [Sketcher::SketchObject] Sketch040
  ArcFitTolerance = 1e-06
  AttachmentSupport = -> [Pad025]
  ExternalGeometry = -> [Pad025]
  FullyConstrained = true
  MakeInternals = false
  MapMode = 5
  Placement = pos=(3,0,0) rot=(0.57735,0.57735,-0.57735;4.18879rad)
  sketch-geometry (10):
    g0: GeomPoint X=-17.55 Y=-54 Z=0
    g1: LineSegment StartX=-17.55 StartY=-59.4848 StartZ=0 EndX=-8.05 EndY=-64.9697 EndZ=0
    g2: LineSegment StartX=-8.05 StartY=-64.9697 StartZ=0 EndX=1.45 EndY=-59.4848 EndZ=0
    g3: LineSegment StartX=1.45 StartY=-59.4848 StartZ=0 EndX=1.45 EndY=-48.5152 EndZ=0
    g4: LineSegment StartX=1.45 StartY=-48.5152 StartZ=0 EndX=-8.05 EndY=-43.0303 EndZ=0
    g5: LineSegment StartX=-8.05 StartY=-43.0303 StartZ=0 EndX=-17.55 EndY=-48.5152 EndZ=0
    g6: LineSegment StartX=-17.55 StartY=-48.5152 StartZ=0 EndX=-17.55 EndY=-59.4848 EndZ=0
    g7: Circle [constr] CenterX=-8.05 CenterY=-54 CenterZ=0 NormalX=0 NormalY=0 NormalZ=1 AngleXU=0 Radius=10.9697
    g8: GeomPoint X=-17.55 Y=-54 Z=0
    g9: Circle CenterX=-8.05 CenterY=-54 CenterZ=0 NormalX=0 NormalY=0 NormalZ=1 AngleXU=0 Radius=4.25
  constraints (20):
    c: Symmetric(g-4,g-4,g0)
    c: Coincident(g1,g2)
    c: Coincident(g2,g3)
    c: Coincident(g3,g4)
    c: Coincident(g4,g5)
    c: Coincident(g5,g6)
    c: Coincident(g6,g1)
    c: Equal(g1, g2-g6) x5
    c: PointOnObject(g1,g7)
    c: PointOnObject(g2,g7)
    c: PointOnObject(g3,g7)
    c: PointOnObject(g4,g7)
    c: PointOnObject(g5,g7)
    c: PointOnObject(g6,g7)
    c: Distance(g3,g6) = 19
    c: Vertical(g3)
    c: Symmetric(g6,g6,g8)
    c: Coincident(g0,g8)
    c: Diameter(g9) = 8.5
    c: Coincident(g9,g7)
FEATURE [PartDesign::Pocket] Pocket011
  BaseFeature = -> Pad025
  Direction = (1,-1.3e-15,0)
  Length = 1
  Length2 = 3
  Placement = pos=(0,0,0) rot=(1,1,1;2.0944rad)
  Profile = -> Sketch040
  ReferenceAxis = -> Sketch040 [N_Axis]
  Suppressed = false
  Type = 4
FEATURE [PartDesign::Pad] Pad026
  BaseFeature = -> Pocket011
  Direction = (-1,0,-2.3e-15)
  Length = 5
  Length2 = 10
  Placement = pos=(0,0,0) rot=(1,1,1;2.0944rad)
  Profile = -> Pocket011 [Face74]
  Suppressed = false
  Type = 0
FEATURE [PartDesign::Body] Body021
  AllowCompound = false
  Group = -> [Sketch035,Pad022,Sketch036,Pocket010,Sketch037,Pad023,LinearPattern,Fillet001,Chamfer011,Fillet002,Hole001,Hole002,Sketch038,Pad024,Fillet003,Sketch039,Pad025,Sketch040,Pocket011,Pad026]
  Origin = -> Origin033
  Placement = pos=(64.7,0,0) rot=(0,0,1;0rad)
  Tip = -> Pad026
FEATURE [App::Part] Part009
  Group = -> [Body021]
  Origin = -> Origin032
  Placement = pos=(-3,0,0) rot=(0,0,1;0rad)
FEATURE [App::Part] Part002  label="Drum_end"
  Group = -> [Body002]
  Origin = -> Origin004
  Placement = pos=(0,0,9.75) rot=(0,0,1;0rad)
FEATURE [PartDesign::Body] Body002
  AllowCompound = false
  Group = -> [Sketch008,Pad008,Sketch010,Pocket,Chamfer003,PolarPattern,Sketch011,Pocket001,Chamfer004,Sketch020,Pad014,Chamfer010]
  Origin = -> Origin005
  Tip = -> Chamfer010
FEATURE [Sketcher::SketchObject] Sketch011
  ArcFitTolerance = 1e-06
  AttachmentSupport = -> [Pocket001]
  FullyConstrained = true
  MakeInternals = false
  MapMode = 5
  Placement = pos=(0,0,5.5) rot=(0,0,1;0rad)
  sketch-geometry (7):
    g0: ArcOfCircle CenterX=0 CenterY=0 CenterZ=0 NormalX=0 NormalY=0 NormalZ=1 AngleXU=0 Radius=16 StartAngle=1.89314 EndAngle=2.50509
    g1: LineSegment [constr] StartX=0 StartY=0 StartZ=0 EndX=-9.40456 EndY=12.9443 EndZ=0
    g2: ArcOfCircle CenterX=-7.9351 CenterY=10.9217 CenterZ=0 NormalX=0 NormalY=0 NormalZ=1 AngleXU=0 Radius=1.5 StartAngle=4.39823 EndAngle=6.28319
    g3: ArcOfCircle CenterX=-11.2585 CenterY=8.32145 CenterZ=0 NormalX=0 NormalY=0 NormalZ=1 AngleXU=0 Radius=2 StartAngle=1.25664 EndAngle=2.50509
    g4: ArcOfCircle CenterX=-4.4351 CenterY=13.2789 CenterZ=0 NormalX=0 NormalY=0 NormalZ=1 AngleXU=0 Radius=2 StartAngle=1.89314 EndAngle=3.14159
    g5: LineSegment StartX=-6.4351 StartY=13.2789 StartZ=0 EndX=-6.4351 EndY=10.9217 EndZ=0
    g6: LineSegment StartX=-8.39863 StartY=9.49514 StartZ=0 EndX=-10.6405 EndY=10.2236 EndZ=0
  constraints (18):
    c: Coincident(g0,g-1)
    c: PointOnObject(g0,g-3)
    c: Coincident(g1,g0)
    c: PointOnObject(g1,g0)
    c: Angle(g-2,g1) = 0.628319
    c: PointOnObject(g2,g1)
    c: Vertical(g5)
    c: Tangent(g6,g3) = -1.5708
    c: Tangent(g6,g2) = 1.5708
    c: Tangent(g5,g2) = 1.5708
    c: Tangent(g5,g4) = -1.5708
    c: Tangent(g3,g0) = -1.5708
    c: Tangent(g4,g0) = -1.5708
    c: Equal(g3,g4)
    c: Equal(g6,g5)
    c: Radius(g2) = 1.5
    c: Distance(g2,g1) = 2.5
    c: Radius(g3) = 2
FEATURE [PartDesign::Pocket] Pocket001  label="MicroSWIndex_Pocket"
  BaseFeature = -> PolarPattern
  Direction = (0,0,-1)
  Length = 5
  Length2 = 5
  Profile = -> Sketch011
  ReferenceAxis = -> Sketch011 [N_Axis]
  Refine = true
  Suppressed = false
  Type = 2
FEATURE [PartDesign::Chamfer] Chamfer004  label="Outer_Chamfer"
  Angle = 45
  Base = -> Pocket001 [Edge62,Edge7,Edge15,Edge16,Edge18,Edge17]
  BaseFeature = -> Pocket001
  ChamferType = 0
  FlipDirection = false
  Refine = true
  Size = 0.2
  Size2 = 1
  SupportTransform = false
  Suppressed = false
  UseAllEdges = false
FEATURE [Sketcher::SketchObject] Sketch020
  ArcFitTolerance = 1e-06
  AttachmentSupport = -> [Pocket001]
  ExternalGeometry = -> [Pocket001]
  FullyConstrained = true
  MakeInternals = false
  MapMode = 5
  Placement = pos=(0,0,5.5) rot=(0,0,1;0rad)
  sketch-geometry (17):
    g0: GeomPoint [constr] X=0 Y=0 Z=0
    g1: LineSegment StartX=-2.55 StartY=-1.55 StartZ=0 EndX=2.55 EndY=-1.55 EndZ=0
    g2: LineSegment StartX=2.55 StartY=-1.55 StartZ=0 EndX=2.55 EndY=1.55 EndZ=0
    g3: LineSegment StartX=2.55 StartY=1.55 StartZ=0 EndX=-2.55 EndY=1.55 EndZ=0
    g4: LineSegment StartX=-2.55 StartY=1.55 StartZ=0 EndX=-2.55 EndY=-1.55 EndZ=0
    g5: GeomPoint [constr] X=0 Y=0 Z=0
    g6: LineSegment StartX=3.5 StartY=3.5 StartZ=0 EndX=-3.5 EndY=3.5 EndZ=0
    g7: LineSegment StartX=-4 StartY=3 StartZ=0 EndX=-4 EndY=-3 EndZ=0
    g8: LineSegment StartX=-3.5 StartY=-3.5 StartZ=0 EndX=3.5 EndY=-3.5 EndZ=0
    g9: LineSegment StartX=4 StartY=-3 StartZ=0 EndX=4 EndY=3 EndZ=0
    g10: ArcOfCircle CenterX=3.5 CenterY=3 CenterZ=0 NormalX=0 NormalY=0 NormalZ=1 AngleXU=0 Radius=0.5 StartAngle=1e-16 EndAngle=1.5708
    g11: ArcOfCircle CenterX=-3.5 CenterY=3 CenterZ=0 NormalX=0 NormalY=0 NormalZ=1 AngleXU=0 Radius=0.5 StartAngle=1.5708 EndAngle=3.14159
    g12: ArcOfCircle CenterX=-3.5 CenterY=-3 CenterZ=0 NormalX=0 NormalY=0 NormalZ=1 AngleXU=0 Radius=0.5 StartAngle=3.14159 EndAngle=4.71239
    g13: ArcOfCircle CenterX=3.5 CenterY=-3 CenterZ=0 NormalX=0 NormalY=0 NormalZ=1 AngleXU=0 Radius=0.5 StartAngle=4.71239 EndAngle=6.28319
    g14: GeomPoint [constr] X=4 Y=3.5 Z=0
    g15: GeomPoint [constr] X=-4 Y=-3.5 Z=0
    g16: LineSegment [constr] StartX=-3.5 StartY=3 StartZ=0 EndX=3.5 EndY=-3 EndZ=0
  constraints (37):
    c: Coincident(g0,g-1)
    c: Coincident(g1,g2)
    c: Coincident(g2,g3)
    c: Coincident(g3,g4)
    c: Coincident(g4,g1)
    c: Horizontal(g1)
    c: Horizontal(g3)
    c: Vertical(g2)
    c: Vertical(g4)
    c: Symmetric(g3,g1,g5)
    c: Coincident(g5,g0)
    c: Coincident(g2,g-3)
    c: Tangent(g6,g10) = -1.5708
    c: Tangent(g6,g11) = -1.5708
    c: Tangent(g7,g11) = -1.5708
    c: Tangent(g7,g12) = -1.5708
    c: Tangent(g8,g12) = -1.5708
    c: Tangent(g8,g13) = -1.5708
    c: Tangent(g9,g13) = -1.5708
    c: Tangent(g9,g10) = -1.5708
    c: Horizontal(g6)
    c: Horizontal(g8)
    c: Vertical(g7)
    c: Vertical(g9)
    c: Equal(g10,g11)
    c: Equal(g11,g12)
    c: Equal(g12,g13)
    c: PointOnObject(g14,g6)
    c: PointOnObject(g14,g9)
    c: PointOnObject(g15,g7)
    c: PointOnObject(g15,g8)
    c: Radius(g11) = 0.5
    c: Distance(g7,g9) = 8
    c: Distance(g8,g6) = 7
    c: Coincident(g16,g11)
    c: Coincident(g16,g13)
    c: Symmetric(g12,g10,g0)
FEATURE [PartDesign::Pad] Pad014  label="Key_Pad"
  BaseFeature = -> Chamfer004
  Direction = (0,0,1)
  Length = 10
  Length2 = 10
  Profile = -> Sketch020
  ReferenceAxis = -> Sketch020 [N_Axis]
  Refine = true
  Suppressed = false
  Type = 0
FEATURE [PartDesign::Chamfer] Chamfer010  label="Key_Chamfer"
  Angle = 45
  Base = -> Pad014 [Face58]
  BaseFeature = -> Pad014
  ChamferType = 0
  FlipDirection = false
  Refine = true
  Size = 0.45
  Size2 = 1
  SupportTransform = false
  Suppressed = false
  UseAllEdges = false
FEATURE [Part::FeaturePython] Clone014  label="Drum_end001"  # Draft clone (typed FeaturePython)
  AttacherType = Attacher::AttachEngine3D
  Fuse = false
  Objects = -> [Part002]
  Placement = pos=(0,0,98.5) rot=(0,0,1;0rad)
  Scale = (1,1,-1)
note: 1 file-system path scrubbed to <path> (originals preserved in the JSON sidecar)
